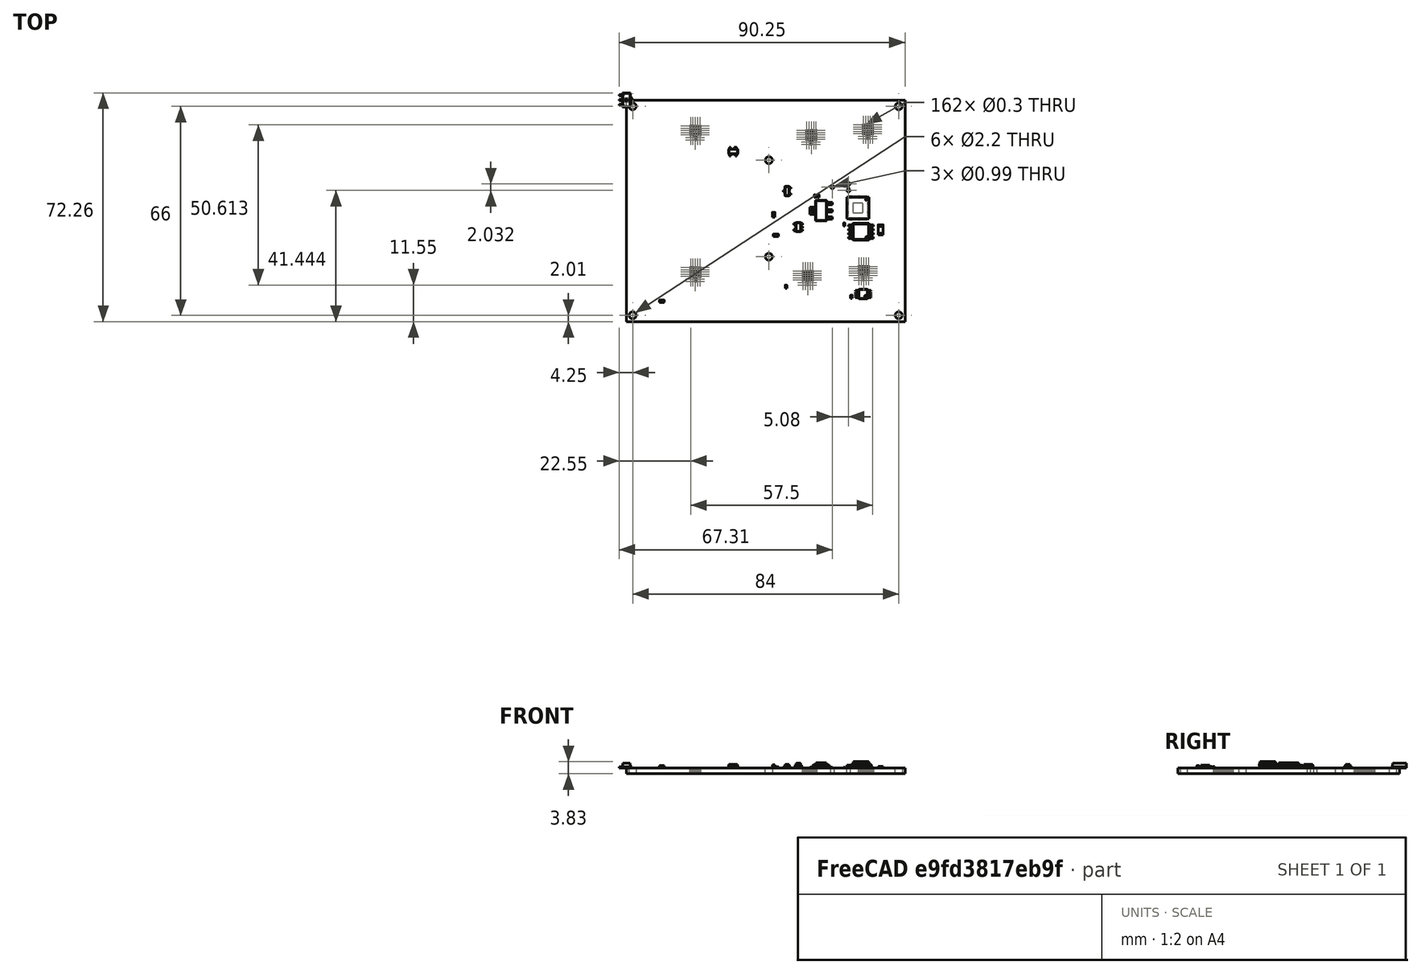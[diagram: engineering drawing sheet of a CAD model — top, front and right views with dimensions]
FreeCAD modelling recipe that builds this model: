
FCSTD DOCUMENT  (FreeCAD 2023.131R26244 +5365 (Git))
Label: FreeCAD_Render
License: All rights reserved
LicenseURL: http://en.wikipedia.org/wiki/All_rights_reserved
objects: App::Link×159, Part::Feature×25, App::Part×10, PartDesign::CoordinateSystem×1, Sketcher::SketchObject×1
note: 28 computed .brp shape members not serialized (recipe doc carries the construction recipe); baked Part::Feature solids carry a one-line shape summary decoded from their .brp

FEATURE [PartDesign::CoordinateSystem] Local_CS_5cf6
  AttacherType = Attacher::AttachEngine3D
  AttachmentSupport = -> [X_Axis]
  FixShape = 1
  InvalidShape = false
  MapMode = 2
  Support = -> [X_Axis]
  TreeRank = 4
  ValidateShape = false
FEATURE [Part::Feature] Pcb_5cf6
  FixShape = 1
  InvalidShape = false
  Placement = pos=(-99,65.045,0) rot=(0,0,1;0rad)
  TreeRank = 17
  ValidateShape = false
  shape: bbox 88 x 70 x 1.77 mm, 177 faces (baked)
FEATURE [Sketcher::SketchObject] PCB_Sketch_5cf6
  ArcFitTolerance = 1e-06
  ExternalBSplineMaxDegree = 5
  ExternalBSplineTolerance = 0.0001
  FixShape = 1
  FullyConstrained = false
  InternalTolerance = 1e-06
  InvalidShape = false
  MakeInternals = false
  TreeRank = 34
  ValidateShape = false
  sketch-geometry (4):
    g0: LineSegment StartX=0 StartY=-0.005 StartZ=0 EndX=88 EndY=-0.005 EndZ=0
    g1: LineSegment StartX=88 StartY=-0.005 StartZ=0 EndX=88 EndY=-70.005 EndZ=0
    g2: LineSegment StartX=88 StartY=-70.005 StartZ=0 EndX=0 EndY=-70.005 EndZ=0
    g3: LineSegment StartX=0 StartY=-70.005 StartZ=0 EndX=0 EndY=-0.005 EndZ=0
  constraints (4):
    c: Coincident(g2,g3)
    c: Coincident(g0,g3)
    c: Coincident(g1,g2)
    c: Coincident(g0,g1)
FEATURE [Part::Feature] Shape  label="R35_R_0402_1005Metric_f5f3ad6d96c7"
  FixShape = 1
  InvalidShape = false
  Placement = pos=(68.8,-39.325,0) rot=(0,0,-1;1.5708rad)
  TreeRank = 40
  ValidateShape = false
  shape: bbox 0.5 x 1 x 0.35 mm, 26 faces (baked)
FEATURE [App::Link] R35_R_0402_1005Metric_f5f3ad6d96c7_ln_  label="R9_R_0402_1005Metric_a21117af0435"
  AutoLinkLabel = true
  AutoPlacement = true
  LinkPlacement = pos=(48.15,-36.3,0) rot=(0,0,-1;1.5708rad)
  LinkedObject = -> Shape
  Placement = pos=(48.15,-36.3,0) rot=(0,0,-1;1.5708rad)
  SyncGroupVisibility = false
  TreeRank = 41
  _LinkVersion = 1
FEATURE [Part::Feature] Shape001  label="U27_MSOP_8_3x3mm_P065mm_f5ce7eb6c5d4"
  FixShape = 1
  InvalidShape = false
  Placement = pos=(74.7875,-61.275,0) rot=(0,0,1;3.14159rad)
  TreeRank = 43
  ValidateShape = false
  shape: bbox 4.9 x 3 x 0.95 mm, 156 faces (baked)
FEATURE [Part::Feature] Shape002  label="C12_C_0603_1608Metric_8642f7516920"
  FixShape = 1
  InvalidShape = false
  Placement = pos=(60.1,-30.35,0) rot=(0,0,1;3.14159rad)
  TreeRank = 45
  ValidateShape = false
  shape: bbox 1.6 x 0.8 x 0.8 mm, 28 faces (baked)
FEATURE [Part::Feature] Shape003  label="C99_C_0402_1005Metric_0b61def5e92b"
  FixShape = 1
  InvalidShape = false
  Placement = pos=(71.05,-62.125,0) rot=(0,0,-1;1.5708rad)
  TreeRank = 47
  ValidateShape = false
  shape: bbox 0.5 x 1 x 0.5 mm, 28 faces (baked)
FEATURE [App::Link] C99_C_0402_1005Metric_0b61def5e92b_ln_  label="C65_C_0402_1005Metric_039dcb1e20b4"
  AutoLinkLabel = true
  AutoPlacement = true
  LinkPlacement = pos=(50.435,-57.05,0) rot=(0,0,1;1.5708rad)
  LinkedObject = -> Shape003
  Placement = pos=(50.435,-57.05,0) rot=(0,0,1;1.5708rad)
  SyncGroupVisibility = false
  TreeRank = 48
  _LinkVersion = 1
FEATURE [App::Link] C12_C_0603_1608Metric_8642f7516920_ln_  label="C7_C_0603_1608Metric_5e726636510c"
  AutoLinkLabel = true
  AutoPlacement = true
  LinkPlacement = pos=(50.4,-40.35,0) rot=(0,0,-1;1.5708rad)
  LinkedObject = -> Shape002
  Placement = pos=(50.4,-40.35,0) rot=(0,0,-1;1.5708rad)
  SyncGroupVisibility = false
  TreeRank = 49
  _LinkVersion = 1
FEATURE [Part::Feature] Shape004  label="L20_L_0402_1005Metric_fefcc591d3d4"
  FixShape = 1
  InvalidShape = false
  Placement = pos=(50.435,-58.95,0) rot=(0,0,1;1.5708rad)
  TreeRank = 51
  ValidateShape = false
  shape: bbox 0.5 x 1 x 0.5 mm, 28 faces (baked)
FEATURE [App::Link] L20_L_0402_1005Metric_fefcc591d3d4_ln_  label="L12_L_0402_1005Metric_9afa7251a08a"
  AutoLinkLabel = true
  AutoPlacement = true
  LinkPlacement = pos=(51.02,-12,0) rot=(0,0,1;0rad)
  LinkedObject = -> Shape004
  Placement = pos=(51.02,-12,0) rot=(0,0,1;0rad)
  SyncGroupVisibility = false
  TreeRank = 52
  _LinkVersion = 1
FEATURE [App::Link] L20_L_0402_1005Metric_fefcc591d3d4_ln_001  label="L18_L_0402_1005Metric_8f30db38a927"
  AutoLinkLabel = true
  AutoPlacement = true
  LinkPlacement = pos=(47.085,-58,0) rot=(0,0,1;0rad)
  LinkedObject = -> Shape004
  Placement = pos=(47.085,-58,0) rot=(0,0,1;0rad)
  SyncGroupVisibility = false
  TreeRank = 53
  _LinkVersion = 1
FEATURE [App::Link] C99_C_0402_1005Metric_0b61def5e92b_ln_001  label="C32_C_0402_1005Metric_a150cae1aaa9"
  AutoLinkLabel = true
  AutoPlacement = true
  LinkPlacement = pos=(49.57,-11.05,0) rot=(0,0,1;1.5708rad)
  LinkedObject = -> Shape003
  Placement = pos=(49.57,-11.05,0) rot=(0,0,1;1.5708rad)
  SyncGroupVisibility = false
  TreeRank = 54
  _LinkVersion = 1
FEATURE [App::Link] C99_C_0402_1005Metric_0b61def5e92b_ln_002  label="C100_C_0402_1005Metric_bd74d8f4673b"
  AutoLinkLabel = true
  AutoPlacement = true
  LinkPlacement = pos=(78.5375,-60.455,0) rot=(0,0,-1;1.5708rad)
  LinkedObject = -> Shape003
  Placement = pos=(78.5375,-60.455,0) rot=(0,0,-1;1.5708rad)
  SyncGroupVisibility = false
  TreeRank = 55
  _LinkVersion = 1
FEATURE [App::Link] L20_L_0402_1005Metric_fefcc591d3d4_ln_002  label="L9_L_0402_1005Metric_ae438e03b951"
  AutoLinkLabel = true
  AutoPlacement = true
  LinkPlacement = pos=(46.22,-12,0) rot=(0,0,1;0rad)
  LinkedObject = -> Shape004
  Placement = pos=(46.22,-12,0) rot=(0,0,1;0rad)
  SyncGroupVisibility = false
  TreeRank = 56
  _LinkVersion = 1
FEATURE [App::Link] C12_C_0603_1608Metric_8642f7516920_ln_001  label="C57_C_0603_1608Metric_56c1fd1c9b26"
  AutoLinkLabel = true
  AutoPlacement = true
  LinkPlacement = pos=(25.875,-53.6,0) rot=(0,0,1;3.14159rad)
  LinkedObject = -> Shape002
  Placement = pos=(25.875,-53.6,0) rot=(0,0,1;3.14159rad)
  SyncGroupVisibility = false
  TreeRank = 57
  _LinkVersion = 1
FEATURE [Part::Feature] Shape005  label="D1_LED_0603_1608Metric_cfe29d252c61"
  FixShape = 1
  InvalidShape = false
  Placement = pos=(46.5,-36.2875,0) rot=(0,0,1;1.5708rad)
  TreeRank = 59
  ValidateShape = false
  shape: bbox 0.8 x 1.6 x 1.1 mm, 50 faces (baked)
FEATURE [Part::Feature] Shape006  label="R7_R_0603_1608Metric_f544fe8919fd"
  FixShape = 1
  InvalidShape = false
  Placement = pos=(47.225,-42.725,0) rot=(0,0,1;0rad)
  TreeRank = 61
  ValidateShape = false
  shape: bbox 1.6 x 0.8 x 0.45 mm, 26 faces (baked)
FEATURE [Part::Feature] Solid  label="adbeea57-9c39-11ed-93f0-dde97e994e83_part"
  FixShape = 1
  InvalidShape = false
  TreeRank = 75
  ValidateShape = false
  shape: bbox 2.5 x 4.5 x 1.5 mm, 12 faces (baked)
FEATURE [App::Part] Part  label="adbeea57-9c39-11ed-93f0-dde97e994e83"
  ClaimAllChildren = false
  ExportMode = 1
  Group = -> [Solid]
  Origin = -> Origin008
  TreeRank = 77
  _ExportChildren = -> [Solid]
  _GroupVersion = 1
FEATURE [Part::Feature] Solid001  label="adbeea58-9c39-11ed-93f0-dde97e994e83_part"
  FixShape = 1
  InvalidShape = false
  TreeRank = 78
  ValidateShape = false
  shape: bbox 2.5 x 1.6 x 0.4 mm, 12 faces (baked)
FEATURE [App::Part] Part001  label="adbeea58-9c39-11ed-93f0-dde97e994e83"
  ClaimAllChildren = false
  ExportMode = 1
  Group = -> [Solid001]
  Origin = -> Origin009
  TreeRank = 80
  _ExportChildren = -> [Solid001]
  _GroupVersion = 1
FEATURE [Part::Feature] Compound  label="adbeea59-9c39-11ed-93f0-dde97e994e83_part"
  FixShape = 1
  InvalidShape = false
  TreeRank = 81
  ValidateShape = false
  shape: bbox 1.5 x 3.4 x 0.4 mm, 18 faces, 3 solids (baked)
FEATURE [App::Part] Part002  label="adbeea59-9c39-11ed-93f0-dde97e994e83"
  ClaimAllChildren = false
  ExportMode = 1
  Group = -> [Compound]
  Origin = -> Origin010
  TreeRank = 83
  _ExportChildren = -> [Compound]
  _GroupVersion = 1
FEATURE [App::Part] Part003  label="adbeea56-9c39-11ed-93f0-dde97e994e83"
  ClaimAllChildren = false
  ExportMode = 1
  Group = -> [Part,Part001,Part002]
  Origin = -> Origin011
  TreeRank = 85
  _ExportChildren = -> [Part,Part001,Part002]
  _GroupVersion = 1
FEATURE [App::Part] Part004  label="U19_CQ assembly_0c48127af4d7"
  ClaimAllChildren = false
  ExportMode = 1
  Group = -> [Part003]
  Origin = -> Origin012
  Placement = pos=(57.3,-56.8,0) rot=(0,0,1;1.5708rad)
  TreeRank = 87
  _ExportChildren = -> [Part003]
  _GroupVersion = 1
FEATURE [Part::Feature] Shape007  label="U9_SOIC_8_5275x5275mm_P127mm_06fe98f0ee27"
  FixShape = 1
  InvalidShape = false
  Placement = pos=(74.1,-41.6,0) rot=(0,0,1;3.14159rad)
  TreeRank = 89
  ValidateShape = false
  shape: bbox 7.9 x 5.275 x 2.055 mm, 156 faces (baked)
FEATURE [App::Link] L20_L_0402_1005Metric_fefcc591d3d4_ln_003  label="L2_L_0402_1005Metric_494311214f8f"
  AutoLinkLabel = true
  AutoPlacement = true
  LinkPlacement = pos=(5.3,-14.185,0) rot=(0,0,1;1.5708rad)
  LinkedObject = -> Shape004
  Placement = pos=(5.3,-14.185,0) rot=(0,0,1;1.5708rad)
  SyncGroupVisibility = false
  TreeRank = 90
  _LinkVersion = 1
FEATURE [Part::Feature] Shape008  label="L6_L_0603_1608Metric_c72d023e8189"
  FixShape = 1
  InvalidShape = false
  Placement = pos=(11.2,-63.6,0) rot=(0,0,1;3.14159rad)
  TreeRank = 92
  ValidateShape = false
  shape: bbox 1.6 x 0.8 x 0.8 mm, 28 faces (baked)
FEATURE [Part::Feature] Shape009  label="U4_SOT_223_62a9cd10a710"
  FixShape = 1
  InvalidShape = false
  Placement = pos=(61.5,-34.95,0) rot=(0,0,1;3.14159rad)
  TreeRank = 94
  ValidateShape = false
  shape: bbox 7 x 6.5 x 1.7 mm, 78 faces (baked)
FEATURE [App::Link] U27_MSOP_8_3x3mm_P065mm_f5ce7eb6c5d4_ln_  label="U22_MSOP_8_3x3mm_P065mm_3038061a7a3b"
  AutoLinkLabel = true
  AutoPlacement = true
  LinkPlacement = pos=(76.3063,-16.625,0) rot=(0,0,1;3.14159rad)
  LinkedObject = -> Shape001
  Placement = pos=(76.3063,-16.625,0) rot=(0,0,1;3.14159rad)
  SyncGroupVisibility = false
  TreeRank = 95
  _LinkVersion = 1
FEATURE [App::Link] R7_R_0603_1608Metric_f544fe8919fd_ln_  label="R16_R_0603_1608Metric_eff10aa3adbc"
  AutoLinkLabel = true
  AutoPlacement = true
  LinkPlacement = pos=(54.025,-42.725,0) rot=(0,0,1;0rad)
  LinkedObject = -> Shape006
  Placement = pos=(54.025,-42.725,0) rot=(0,0,1;0rad)
  SyncGroupVisibility = false
  TreeRank = 96
  _LinkVersion = 1
FEATURE [App::Link] C99_C_0402_1005Metric_0b61def5e92b_ln_003  label="C72_C_0402_1005Metric_0a341764582e"
  AutoLinkLabel = true
  AutoPlacement = true
  LinkPlacement = pos=(18.3,-12.6,0) rot=(0,0,1;3.14159rad)
  LinkedObject = -> Shape003
  Placement = pos=(18.3,-12.6,0) rot=(0,0,1;3.14159rad)
  SyncGroupVisibility = false
  TreeRank = 97
  _LinkVersion = 1
FEATURE [App::Link] C99_C_0402_1005Metric_0b61def5e92b_ln_004  label="C42_C_0402_1005Metric_1668cc783fed"
  AutoLinkLabel = true
  AutoPlacement = true
  LinkPlacement = pos=(37.5,-57.9,0) rot=(0,0,1;0rad)
  LinkedObject = -> Shape003
  Placement = pos=(37.5,-57.9,0) rot=(0,0,1;0rad)
  SyncGroupVisibility = false
  TreeRank = 98
  _LinkVersion = 1
FEATURE [App::Link] C99_C_0402_1005Metric_0b61def5e92b_ln_005  label="C61_C_0402_1005Metric_119fb7f471d7"
  AutoLinkLabel = true
  AutoPlacement = true
  LinkPlacement = pos=(44.185,-58,0) rot=(0,0,1;0rad)
  LinkedObject = -> Shape003
  Placement = pos=(44.185,-58,0) rot=(0,0,1;0rad)
  SyncGroupVisibility = false
  TreeRank = 99
  _LinkVersion = 1
FEATURE [App::Link] R35_R_0402_1005Metric_f5f3ad6d96c7_ln_001  label="R12_R_0402_1005Metric_454fa87694b6"
  AutoLinkLabel = true
  AutoPlacement = true
  LinkPlacement = pos=(45.15,-33.2375,0) rot=(0,0,-1;1.5708rad)
  LinkedObject = -> Shape
  Placement = pos=(45.15,-33.2375,0) rot=(0,0,-1;1.5708rad)
  SyncGroupVisibility = false
  TreeRank = 100
  _LinkVersion = 1
FEATURE [App::Link] C99_C_0402_1005Metric_0b61def5e92b_ln_006  label="C41_C_0402_1005Metric_b9c80529164f"
  AutoLinkLabel = true
  AutoPlacement = true
  LinkPlacement = pos=(36.68,-12,0) rot=(0,0,1;0rad)
  LinkedObject = -> Shape003
  Placement = pos=(36.68,-12,0) rot=(0,0,1;0rad)
  SyncGroupVisibility = false
  TreeRank = 101
  _LinkVersion = 1
FEATURE [App::Link] L20_L_0402_1005Metric_fefcc591d3d4_ln_004  label="L17_L_0402_1005Metric_c09bc69e0e8d"
  AutoLinkLabel = true
  AutoPlacement = true
  LinkPlacement = pos=(45.635,-58.95,0) rot=(0,0,1;1.5708rad)
  LinkedObject = -> Shape004
  Placement = pos=(45.635,-58.95,0) rot=(0,0,1;1.5708rad)
  SyncGroupVisibility = false
  TreeRank = 102
  _LinkVersion = 1
FEATURE [App::Link] L20_L_0402_1005Metric_fefcc591d3d4_ln_005  label="L35_L_0402_1005Metric_862772697643"
  AutoLinkLabel = true
  AutoPlacement = true
  LinkPlacement = pos=(12.57,-55.965,0) rot=(0,0,1;1.5708rad)
  LinkedObject = -> Shape004
  Placement = pos=(12.57,-55.965,0) rot=(0,0,1;1.5708rad)
  SyncGroupVisibility = false
  TreeRank = 103
  _LinkVersion = 1
FEATURE [App::Link] C99_C_0402_1005Metric_0b61def5e92b_ln_007  label="C94_C_0402_1005Metric_5b9e6d4c6d4e"
  AutoLinkLabel = true
  AutoPlacement = true
  LinkPlacement = pos=(12.57,-58.63,0) rot=(0,0,1;1.5708rad)
  LinkedObject = -> Shape003
  Placement = pos=(12.57,-58.63,0) rot=(0,0,1;1.5708rad)
  SyncGroupVisibility = false
  TreeRank = 104
  _LinkVersion = 1
FEATURE [App::Link] C99_C_0402_1005Metric_0b61def5e92b_ln_008  label="C17_C_0402_1005Metric_572786f3d237"
  AutoLinkLabel = true
  AutoPlacement = true
  LinkPlacement = pos=(66.78,-44.5,0) rot=(0,0,1;0rad)
  LinkedObject = -> Shape003
  Placement = pos=(66.78,-44.5,0) rot=(0,0,1;0rad)
  SyncGroupVisibility = false
  TreeRank = 105
  _LinkVersion = 1
FEATURE [App::Link] R35_R_0402_1005Metric_f5f3ad6d96c7_ln_002  label="R15_R_0402_1005Metric_dd92e1eecf5b"
  AutoLinkLabel = true
  AutoPlacement = true
  LinkPlacement = pos=(54.15,-33.2775,0) rot=(0,0,-1;1.5708rad)
  LinkedObject = -> Shape
  Placement = pos=(54.15,-33.2775,0) rot=(0,0,-1;1.5708rad)
  SyncGroupVisibility = false
  TreeRank = 106
  _LinkVersion = 1
FEATURE [App::Link] C12_C_0603_1608Metric_8642f7516920_ln_002  label="C16_C_0603_1608Metric_42011b40d980"
  AutoLinkLabel = true
  AutoPlacement = true
  LinkPlacement = pos=(6.3,-15.9,0) rot=(0,0,1;3.14159rad)
  LinkedObject = -> Shape002
  Placement = pos=(6.3,-15.9,0) rot=(0,0,1;3.14159rad)
  SyncGroupVisibility = false
  TreeRank = 107
  _LinkVersion = 1
FEATURE [App::Link] C99_C_0402_1005Metric_0b61def5e92b_ln_009  label="C38_C_0402_1005Metric_071abb743ee5"
  AutoLinkLabel = true
  AutoPlacement = true
  LinkPlacement = pos=(26.4,-12.6,0) rot=(0,0,1;3.14159rad)
  LinkedObject = -> Shape003
  Placement = pos=(26.4,-12.6,0) rot=(0,0,1;3.14159rad)
  SyncGroupVisibility = false
  TreeRank = 108
  _LinkVersion = 1
FEATURE [App::Link] L20_L_0402_1005Metric_fefcc591d3d4_ln_006  label="L28_L_0402_1005Metric_31be49f92a08"
  AutoLinkLabel = true
  AutoPlacement = true
  LinkPlacement = pos=(9.6,-35,0) rot=(0,0,1;0rad)
  LinkedObject = -> Shape004
  Placement = pos=(9.6,-35,0) rot=(0,0,1;0rad)
  SyncGroupVisibility = false
  TreeRank = 109
  _LinkVersion = 1
FEATURE [App::Link] L20_L_0402_1005Metric_fefcc591d3d4_ln_007  label="L16_L_0402_1005Metric_a015a0d61d6a"
  AutoLinkLabel = true
  AutoPlacement = true
  LinkPlacement = pos=(42.285,-58,0) rot=(0,0,1;0rad)
  LinkedObject = -> Shape004
  Placement = pos=(42.285,-58,0) rot=(0,0,1;0rad)
  SyncGroupVisibility = false
  TreeRank = 110
  _LinkVersion = 1
FEATURE [App::Link] C99_C_0402_1005Metric_0b61def5e92b_ln_010  label="C91_C_0402_1005Metric_d935b4825f22"
  AutoLinkLabel = true
  AutoPlacement = true
  LinkPlacement = pos=(11.05,-34.52,0) rot=(0,0,1;1.5708rad)
  LinkedObject = -> Shape003
  Placement = pos=(11.05,-34.52,0) rot=(0,0,1;1.5708rad)
  SyncGroupVisibility = false
  TreeRank = 111
  _LinkVersion = 1
FEATURE [App::Link] C12_C_0603_1608Metric_8642f7516920_ln_003  label="C10_C_0603_1608Metric_9efa6503c595"
  AutoLinkLabel = true
  AutoPlacement = true
  LinkPlacement = pos=(53.4625,-28.575,0) rot=(0,0,1;1.5708rad)
  LinkedObject = -> Shape002
  Placement = pos=(53.4625,-28.575,0) rot=(0,0,1;1.5708rad)
  SyncGroupVisibility = false
  TreeRank = 112
  _LinkVersion = 1
FEATURE [App::Link] R35_R_0402_1005Metric_f5f3ad6d96c7_ln_003  label="R24_R_0402_1005Metric_d04b1966e5ee"
  AutoLinkLabel = true
  AutoPlacement = true
  LinkPlacement = pos=(12.8,-36.51,0) rot=(0,0,1;1.5708rad)
  LinkedObject = -> Shape
  Placement = pos=(12.8,-36.51,0) rot=(0,0,1;1.5708rad)
  SyncGroupVisibility = false
  TreeRank = 113
  _LinkVersion = 1
FEATURE [App::Link] L20_L_0402_1005Metric_fefcc591d3d4_ln_008  label="L32_L_0402_1005Metric_198f0760abc9"
  AutoLinkLabel = true
  AutoPlacement = true
  LinkPlacement = pos=(6.885,-57.3,0) rot=(0,0,1;0rad)
  LinkedObject = -> Shape004
  Placement = pos=(6.885,-57.3,0) rot=(0,0,1;0rad)
  SyncGroupVisibility = false
  TreeRank = 114
  _LinkVersion = 1
FEATURE [App::Link] L20_L_0402_1005Metric_fefcc591d3d4_ln_009  label="L3_L_0402_1005Metric_fcb539355568"
  AutoLinkLabel = true
  AutoPlacement = true
  LinkPlacement = pos=(24.9,-12.115,0) rot=(0,0,-1;1.5708rad)
  LinkedObject = -> Shape004
  Placement = pos=(24.9,-12.115,0) rot=(0,0,-1;1.5708rad)
  SyncGroupVisibility = false
  TreeRank = 115
  _LinkVersion = 1
FEATURE [App::Link] C99_C_0402_1005Metric_0b61def5e92b_ln_011  label="C64_C_0402_1005Metric_0c6ecc967038"
  AutoLinkLabel = true
  AutoPlacement = true
  LinkPlacement = pos=(48.985,-58,0) rot=(0,0,1;0rad)
  LinkedObject = -> Shape003
  Placement = pos=(48.985,-58,0) rot=(0,0,1;0rad)
  SyncGroupVisibility = false
  TreeRank = 116
  _LinkVersion = 1
FEATURE [App::Link] U19_CQ_assembly_0c48127af4d7_ln_  label="U15_CQ assembly_a8ecb2b2cfc9"
  AutoLinkLabel = true
  AutoPlacement = true
  LinkPlacement = pos=(76.3,-10.55,0) rot=(0,0,1;1.5708rad)
  LinkedObject = -> Part004
  Placement = pos=(76.3,-10.55,0) rot=(0,0,1;1.5708rad)
  SyncGroupVisibility = false
  TreeRank = 117
  _LinkVersion = 1
FEATURE [App::Link] C12_C_0603_1608Metric_8642f7516920_ln_004  label="C56_C_0603_1608Metric_def960d6d94d"
  AutoLinkLabel = true
  AutoPlacement = true
  LinkPlacement = pos=(80.375,-7.265,0) rot=(0,0,1;3.14159rad)
  LinkedObject = -> Shape002
  Placement = pos=(80.375,-7.265,0) rot=(0,0,1;3.14159rad)
  SyncGroupVisibility = false
  TreeRank = 118
  _LinkVersion = 1
FEATURE [App::Link] R35_R_0402_1005Metric_f5f3ad6d96c7_ln_004  label="R18_R_0402_1005Metric_c2070ab9652d"
  AutoLinkLabel = true
  AutoPlacement = true
  LinkPlacement = pos=(81.6,-18.11,0) rot=(0,0,1;1.5708rad)
  LinkedObject = -> Shape
  Placement = pos=(81.6,-18.11,0) rot=(0,0,1;1.5708rad)
  SyncGroupVisibility = false
  TreeRank = 119
  _LinkVersion = 1
FEATURE [App::Link] C99_C_0402_1005Metric_0b61def5e92b_ln_012  label="C15_C_0402_1005Metric_dfbf553078c1"
  AutoLinkLabel = true
  AutoPlacement = true
  LinkPlacement = pos=(68.7,-43.98,0) rot=(0,0,-1;1.5708rad)
  LinkedObject = -> Shape003
  Placement = pos=(68.7,-43.98,0) rot=(0,0,-1;1.5708rad)
  SyncGroupVisibility = false
  TreeRank = 120
  _LinkVersion = 1
FEATURE [App::Link] D1_LED_0603_1608Metric_cfe29d252c61_ln_  label="D2_LED_0603_1608Metric_e46dc4190c8f"
  AutoLinkLabel = true
  AutoPlacement = true
  LinkPlacement = pos=(49.5,-36.2875,0) rot=(0,0,1;1.5708rad)
  LinkedObject = -> Shape005
  Placement = pos=(49.5,-36.2875,0) rot=(0,0,1;1.5708rad)
  SyncGroupVisibility = false
  TreeRank = 121
  _LinkVersion = 1
FEATURE [App::Link] L20_L_0402_1005Metric_fefcc591d3d4_ln_010  label="L10_L_0402_1005Metric_c9969f9a3005"
  AutoLinkLabel = true
  AutoPlacement = true
  LinkPlacement = pos=(78.01,-56.7925,0) rot=(0,0,-1;1.5708rad)
  LinkedObject = -> Shape004
  Placement = pos=(78.01,-56.7925,0) rot=(0,0,-1;1.5708rad)
  SyncGroupVisibility = false
  TreeRank = 122
  _LinkVersion = 1
FEATURE [App::Link] L20_L_0402_1005Metric_fefcc591d3d4_ln_011  label="L37_L_0402_1005Metric_2736a4dceb44"
  AutoLinkLabel = true
  AutoPlacement = true
  LinkPlacement = pos=(15.17,-55.965,0) rot=(0,0,1;1.5708rad)
  LinkedObject = -> Shape004
  Placement = pos=(15.17,-55.965,0) rot=(0,0,1;1.5708rad)
  SyncGroupVisibility = false
  TreeRank = 123
  _LinkVersion = 1
FEATURE [App::Link] C12_C_0603_1608Metric_8642f7516920_ln_005  label="C9_C_0603_1608Metric_568df7630068"
  AutoLinkLabel = true
  AutoPlacement = true
  LinkPlacement = pos=(64.425,-30.35,0) rot=(0,0,1;0rad)
  LinkedObject = -> Shape002
  Placement = pos=(64.425,-30.35,0) rot=(0,0,1;0rad)
  SyncGroupVisibility = false
  TreeRank = 124
  _LinkVersion = 1
FEATURE [App::Link] C99_C_0402_1005Metric_0b61def5e92b_ln_013  label="C63_C_0402_1005Metric_87cdc0513b1c"
  AutoLinkLabel = true
  AutoPlacement = true
  LinkPlacement = pos=(72.75,-12.0394,0) rot=(0,0,-1;0.785398rad)
  LinkedObject = -> Shape003
  Placement = pos=(72.75,-12.0394,0) rot=(0,0,-1;0.785398rad)
  SyncGroupVisibility = false
  TreeRank = 125
  _LinkVersion = 1
FEATURE [App::Link] L20_L_0402_1005Metric_fefcc591d3d4_ln_012  label="L22_L_0402_1005Metric_491585082001"
  AutoLinkLabel = true
  AutoPlacement = true
  LinkPlacement = pos=(11.255,-12.6,0) rot=(0,0,1;0rad)
  LinkedObject = -> Shape004
  Placement = pos=(11.255,-12.6,0) rot=(0,0,1;0rad)
  SyncGroupVisibility = false
  TreeRank = 126
  _LinkVersion = 1
FEATURE [App::Link] C12_C_0603_1608Metric_8642f7516920_ln_006  label="C101_C_0603_1608Metric_0d3315560940"
  AutoLinkLabel = true
  AutoPlacement = true
  LinkPlacement = pos=(6.325,-62.1,0) rot=(0,0,1;3.14159rad)
  LinkedObject = -> Shape002
  Placement = pos=(6.325,-62.1,0) rot=(0,0,1;3.14159rad)
  SyncGroupVisibility = false
  TreeRank = 127
  _LinkVersion = 1
FEATURE [App::Link] D1_LED_0603_1608Metric_cfe29d252c61_ln_001  label="D6_LED_0603_1608Metric_c5920ca47e15"
  AutoLinkLabel = true
  AutoPlacement = true
  LinkPlacement = pos=(49.5,-33.25,0) rot=(0,0,1;1.5708rad)
  LinkedObject = -> Shape005
  Placement = pos=(49.5,-33.25,0) rot=(0,0,1;1.5708rad)
  SyncGroupVisibility = false
  TreeRank = 128
  _LinkVersion = 1
FEATURE [App::Link] R7_R_0603_1608Metric_f544fe8919fd_ln_001  label="R6_R_0603_1608Metric_ad8729a0a211"
  AutoLinkLabel = true
  AutoPlacement = true
  LinkPlacement = pos=(58.8,-40.3,0) rot=(0,0,-1;1.5708rad)
  LinkedObject = -> Shape006
  Placement = pos=(58.8,-40.3,0) rot=(0,0,-1;1.5708rad)
  SyncGroupVisibility = false
  TreeRank = 129
  _LinkVersion = 1
FEATURE [App::Link] C99_C_0402_1005Metric_0b61def5e92b_ln_014  label="C85_C_0402_1005Metric_55c8310b5d15"
  AutoLinkLabel = true
  AutoPlacement = true
  LinkPlacement = pos=(72.5687,-17.475,0) rot=(0,0,-1;1.5708rad)
  LinkedObject = -> Shape003
  Placement = pos=(72.5687,-17.475,0) rot=(0,0,-1;1.5708rad)
  SyncGroupVisibility = false
  TreeRank = 130
  _LinkVersion = 1
FEATURE [App::Link] L20_L_0402_1005Metric_fefcc591d3d4_ln_013  label="L19_L_0402_1005Metric_5587f70061e4"
  AutoLinkLabel = true
  AutoPlacement = true
  LinkPlacement = pos=(79.7,-12.115,0) rot=(0,0,-1;1.5708rad)
  LinkedObject = -> Shape004
  Placement = pos=(79.7,-12.115,0) rot=(0,0,-1;1.5708rad)
  SyncGroupVisibility = false
  TreeRank = 131
  _LinkVersion = 1
FEATURE [App::Link] C12_C_0603_1608Metric_8642f7516920_ln_007  label="C5_C_0603_1608Metric_b7c57633a563"
  AutoLinkLabel = true
  AutoPlacement = true
  LinkPlacement = pos=(25.875,-8.9,0) rot=(0,0,1;3.14159rad)
  LinkedObject = -> Shape002
  Placement = pos=(25.875,-8.9,0) rot=(0,0,1;3.14159rad)
  SyncGroupVisibility = false
  TreeRank = 132
  _LinkVersion = 1
FEATURE [App::Link] L20_L_0402_1005Metric_fefcc591d3d4_ln_014  label="L27_L_0402_1005Metric_34f9cab72f46"
  AutoLinkLabel = true
  AutoPlacement = true
  LinkPlacement = pos=(6.7,-35,0) rot=(0,0,1;0rad)
  LinkedObject = -> Shape004
  Placement = pos=(6.7,-35,0) rot=(0,0,1;0rad)
  SyncGroupVisibility = false
  TreeRank = 133
  _LinkVersion = 1
FEATURE [App::Link] C12_C_0603_1608Metric_8642f7516920_ln_008  label="C87_C_0603_1608Metric_3d10d2c6202e"
  AutoLinkLabel = true
  AutoPlacement = true
  LinkPlacement = pos=(79.025,-55.0725,0) rot=(0,0,1;3.14159rad)
  LinkedObject = -> Shape002
  Placement = pos=(79.025,-55.0725,0) rot=(0,0,1;3.14159rad)
  SyncGroupVisibility = false
  TreeRank = 134
  _LinkVersion = 1
FEATURE [App::Link] L20_L_0402_1005Metric_fefcc591d3d4_ln_015  label="L13_L_0402_1005Metric_fe637daa8a0d"
  AutoLinkLabel = true
  AutoPlacement = true
  LinkPlacement = pos=(6.885,-12.6,0) rot=(0,0,1;0rad)
  LinkedObject = -> Shape004
  Placement = pos=(6.885,-12.6,0) rot=(0,0,1;0rad)
  SyncGroupVisibility = false
  TreeRank = 135
  _LinkVersion = 1
FEATURE [App::Link] C12_C_0603_1608Metric_8642f7516920_ln_009  label="C40_C_0603_1608Metric_611b7b94bbb0"
  AutoLinkLabel = true
  AutoPlacement = true
  LinkPlacement = pos=(25.875,-52.1,0) rot=(0,0,1;3.14159rad)
  LinkedObject = -> Shape002
  Placement = pos=(25.875,-52.1,0) rot=(0,0,1;3.14159rad)
  SyncGroupVisibility = false
  TreeRank = 136
  _LinkVersion = 1
FEATURE [App::Link] R35_R_0402_1005Metric_f5f3ad6d96c7_ln_005  label="R38_R_0402_1005Metric_850526eb3a70"
  AutoLinkLabel = true
  AutoPlacement = true
  LinkPlacement = pos=(80.0813,-62.76,0) rot=(0,0,1;1.5708rad)
  LinkedObject = -> Shape
  Placement = pos=(80.0813,-62.76,0) rot=(0,0,1;1.5708rad)
  SyncGroupVisibility = false
  TreeRank = 137
  _LinkVersion = 1
FEATURE [App::Link] C99_C_0402_1005Metric_0b61def5e92b_ln_015  label="C93_C_0402_1005Metric_9b432eb8458a"
  AutoLinkLabel = true
  AutoPlacement = true
  LinkPlacement = pos=(9.97,-58.63,0) rot=(0,0,1;1.5708rad)
  LinkedObject = -> Shape003
  Placement = pos=(9.97,-58.63,0) rot=(0,0,1;1.5708rad)
  SyncGroupVisibility = false
  TreeRank = 138
  _LinkVersion = 1
FEATURE [App::Link] C12_C_0603_1608Metric_8642f7516920_ln_010  label="C60_C_0603_1608Metric_aafec61e4182"
  AutoLinkLabel = true
  AutoPlacement = true
  LinkPlacement = pos=(25.875,-55.1,0) rot=(0,0,1;3.14159rad)
  LinkedObject = -> Shape002
  Placement = pos=(25.875,-55.1,0) rot=(0,0,1;3.14159rad)
  SyncGroupVisibility = false
  TreeRank = 139
  _LinkVersion = 1
FEATURE [App::Link] C12_C_0603_1608Metric_8642f7516920_ln_011  label="C74_C_0603_1608Metric_09ec40bea9be"
  AutoLinkLabel = true
  AutoPlacement = true
  LinkPlacement = pos=(62.565,-9.135,0) rot=(0,0,1;3.14159rad)
  LinkedObject = -> Shape002
  Placement = pos=(62.565,-9.135,0) rot=(0,0,1;3.14159rad)
  SyncGroupVisibility = false
  TreeRank = 140
  _LinkVersion = 1
FEATURE [App::Link] C12_C_0603_1608Metric_8642f7516920_ln_012  label="C102_C_0603_1608Metric_fbca4f1203a4"
  AutoLinkLabel = true
  AutoPlacement = true
  LinkPlacement = pos=(6.325,-60.6,0) rot=(0,0,1;3.14159rad)
  LinkedObject = -> Shape002
  Placement = pos=(6.325,-60.6,0) rot=(0,0,1;3.14159rad)
  SyncGroupVisibility = false
  TreeRank = 141
  _LinkVersion = 1
FEATURE [App::Link] C99_C_0402_1005Metric_0b61def5e92b_ln_016  label="C95_C_0402_1005Metric_b8fe9a8e5a91"
  AutoLinkLabel = true
  AutoPlacement = true
  LinkPlacement = pos=(15.17,-58.63,0) rot=(0,0,1;1.5708rad)
  LinkedObject = -> Shape003
  Placement = pos=(15.17,-58.63,0) rot=(0,0,1;1.5708rad)
  SyncGroupVisibility = false
  TreeRank = 142
  _LinkVersion = 1
FEATURE [App::Link] D1_LED_0603_1608Metric_cfe29d252c61_ln_002  label="D8_LED_0603_1608Metric_bad8365d5fa2"
  AutoLinkLabel = true
  AutoPlacement = true
  LinkPlacement = pos=(55.5,-33.25,0) rot=(0,0,1;1.5708rad)
  LinkedObject = -> Shape005
  Placement = pos=(55.5,-33.25,0) rot=(0,0,1;1.5708rad)
  SyncGroupVisibility = false
  TreeRank = 143
  _LinkVersion = 1
FEATURE [App::Link] C99_C_0402_1005Metric_0b61def5e92b_ln_017  label="C89_C_0402_1005Metric_912ed4a3e6aa"
  AutoLinkLabel = true
  AutoPlacement = true
  LinkPlacement = pos=(5.25,-34.52,0) rot=(0,0,1;1.5708rad)
  LinkedObject = -> Shape003
  Placement = pos=(5.25,-34.52,0) rot=(0,0,1;1.5708rad)
  SyncGroupVisibility = false
  TreeRank = 144
  _LinkVersion = 1
FEATURE [App::Link] L20_L_0402_1005Metric_fefcc591d3d4_ln_016  label="L30_L_0402_1005Metric_7c5d0824e401"
  AutoLinkLabel = true
  AutoPlacement = true
  LinkPlacement = pos=(15.17,-11.265,0) rot=(0,0,1;1.5708rad)
  LinkedObject = -> Shape004
  Placement = pos=(15.17,-11.265,0) rot=(0,0,1;1.5708rad)
  SyncGroupVisibility = false
  TreeRank = 145
  _LinkVersion = 1
FEATURE [App::Link] L20_L_0402_1005Metric_fefcc591d3d4_ln_017  label="L7_L_0402_1005Metric_456bcb2105ab"
  AutoLinkLabel = true
  AutoPlacement = true
  LinkPlacement = pos=(44.77,-12.95,0) rot=(0,0,1;1.5708rad)
  LinkedObject = -> Shape004
  Placement = pos=(44.77,-12.95,0) rot=(0,0,1;1.5708rad)
  SyncGroupVisibility = false
  TreeRank = 146
  _LinkVersion = 1
FEATURE [App::Link] C12_C_0603_1608Metric_8642f7516920_ln_013  label="C76_C_0603_1608Metric_3a528c4e4e0e"
  AutoLinkLabel = true
  AutoPlacement = true
  LinkPlacement = pos=(61.375,-56.7,0) rot=(0,0,1;3.14159rad)
  LinkedObject = -> Shape002
  Placement = pos=(61.375,-56.7,0) rot=(0,0,1;3.14159rad)
  SyncGroupVisibility = false
  TreeRank = 147
  _LinkVersion = 1
FEATURE [App::Link] C99_C_0402_1005Metric_0b61def5e92b_ln_018  label="C4_C_0402_1005Metric_44e2dd5ad2b2"
  AutoLinkLabel = true
  AutoPlacement = true
  LinkPlacement = pos=(8.7,-12.6,0) rot=(0,0,1;3.14159rad)
  LinkedObject = -> Shape003
  Placement = pos=(8.7,-12.6,0) rot=(0,0,1;3.14159rad)
  SyncGroupVisibility = false
  TreeRank = 148
  _LinkVersion = 1
FEATURE [App::Link] R35_R_0402_1005Metric_f5f3ad6d96c7_ln_006  label="R25_R_0402_1005Metric_d01a4dbf24dd"
  AutoLinkLabel = true
  AutoPlacement = true
  LinkPlacement = pos=(11.3,-37,0) rot=(0,0,1;0rad)
  LinkedObject = -> Shape
  Placement = pos=(11.3,-37,0) rot=(0,0,1;0rad)
  SyncGroupVisibility = false
  TreeRank = 149
  _LinkVersion = 1
FEATURE [App::Link] C99_C_0402_1005Metric_0b61def5e92b_ln_019  label="C62_C_0402_1005Metric_ef4612ef1b06"
  AutoLinkLabel = true
  AutoPlacement = true
  LinkPlacement = pos=(45.635,-57.05,0) rot=(0,0,1;1.5708rad)
  LinkedObject = -> Shape003
  Placement = pos=(45.635,-57.05,0) rot=(0,0,1;1.5708rad)
  SyncGroupVisibility = false
  TreeRank = 150
  _LinkVersion = 1
FEATURE [App::Link] C99_C_0402_1005Metric_0b61def5e92b_ln_020  label="C67_C_0402_1005Metric_c4b910a4755d"
  AutoLinkLabel = true
  AutoPlacement = true
  LinkPlacement = pos=(53.785,-58,0) rot=(0,0,1;0rad)
  LinkedObject = -> Shape003
  Placement = pos=(53.785,-58,0) rot=(0,0,1;0rad)
  SyncGroupVisibility = false
  TreeRank = 151
  _LinkVersion = 1
FEATURE [Part::Feature] Shape010  label="F1_Fuse_1206_3216Metric_ddd44b4a31ef"
  FixShape = 1
  InvalidShape = false
  Placement = pos=(80.3,-41,0) rot=(0,0,-1;1.5708rad)
  TreeRank = 153
  ValidateShape = false
  shape: bbox 1.6 x 3.2 x 0.55 mm, 26 faces (baked)
FEATURE [App::Link] L20_L_0402_1005Metric_fefcc591d3d4_ln_018  label="L26_L_0402_1005Metric_0ac06aa6dc64"
  AutoLinkLabel = true
  AutoPlacement = true
  LinkPlacement = pos=(60.4,-58.415,0) rot=(0,0,-1;1.5708rad)
  LinkedObject = -> Shape004
  Placement = pos=(60.4,-58.415,0) rot=(0,0,-1;1.5708rad)
  SyncGroupVisibility = false
  TreeRank = 154
  _LinkVersion = 1
FEATURE [App::Link] C99_C_0402_1005Metric_0b61def5e92b_ln_021  label="C96_C_0402_1005Metric_12cca5f82af4"
  AutoLinkLabel = true
  AutoPlacement = true
  LinkPlacement = pos=(18.3,-57.3,0) rot=(0,0,1;3.14159rad)
  LinkedObject = -> Shape003
  Placement = pos=(18.3,-57.3,0) rot=(0,0,1;3.14159rad)
  SyncGroupVisibility = false
  TreeRank = 155
  _LinkVersion = 1
FEATURE [App::Link] C99_C_0402_1005Metric_0b61def5e92b_ln_022  label="C97_C_0402_1005Metric_f17c20ed1adf"
  AutoLinkLabel = true
  AutoPlacement = true
  LinkPlacement = pos=(77.3,-28.5,0) rot=(0,0,1;1.5708rad)
  LinkedObject = -> Shape003
  Placement = pos=(77.3,-28.5,0) rot=(0,0,1;1.5708rad)
  SyncGroupVisibility = false
  TreeRank = 156
  _LinkVersion = 1
FEATURE [App::Link] L20_L_0402_1005Metric_fefcc591d3d4_ln_019  label="L14_L_0402_1005Metric_1540f4a361fb"
  AutoLinkLabel = true
  AutoPlacement = true
  LinkPlacement = pos=(9.97,-11.265,0) rot=(0,0,1;1.5708rad)
  LinkedObject = -> Shape004
  Placement = pos=(9.97,-11.265,0) rot=(0,0,1;1.5708rad)
  SyncGroupVisibility = false
  TreeRank = 157
  _LinkVersion = 1
FEATURE [App::Link] C99_C_0402_1005Metric_0b61def5e92b_ln_023  label="C92_C_0402_1005Metric_180eef45c809"
  AutoLinkLabel = true
  AutoPlacement = true
  LinkPlacement = pos=(8.7,-57.3,0) rot=(0,0,1;3.14159rad)
  LinkedObject = -> Shape003
  Placement = pos=(8.7,-57.3,0) rot=(0,0,1;3.14159rad)
  SyncGroupVisibility = false
  TreeRank = 158
  _LinkVersion = 1
FEATURE [App::Link] R35_R_0402_1005Metric_f5f3ad6d96c7_ln_007  label="R13_R_0402_1005Metric_2d540afb9262"
  AutoLinkLabel = true
  AutoPlacement = true
  LinkPlacement = pos=(48.15,-33.2875,0) rot=(0,0,-1;1.5708rad)
  LinkedObject = -> Shape
  Placement = pos=(48.15,-33.2875,0) rot=(0,0,-1;1.5708rad)
  SyncGroupVisibility = false
  TreeRank = 159
  _LinkVersion = 1
FEATURE [App::Link] C99_C_0402_1005Metric_0b61def5e92b_ln_024  label="C30_C_0402_1005Metric_0f836c2fbbcc"
  AutoLinkLabel = true
  AutoPlacement = true
  LinkPlacement = pos=(44.77,-11.05,0) rot=(0,0,1;1.5708rad)
  LinkedObject = -> Shape003
  Placement = pos=(44.77,-11.05,0) rot=(0,0,1;1.5708rad)
  SyncGroupVisibility = false
  TreeRank = 160
  _LinkVersion = 1
FEATURE [App::Link] L20_L_0402_1005Metric_fefcc591d3d4_ln_020  label="L21_L_0402_1005Metric_c7900d6e66f0"
  AutoLinkLabel = true
  AutoPlacement = true
  LinkPlacement = pos=(51.885,-58,0) rot=(0,0,1;0rad)
  LinkedObject = -> Shape004
  Placement = pos=(51.885,-58,0) rot=(0,0,1;0rad)
  SyncGroupVisibility = false
  TreeRank = 161
  _LinkVersion = 1
FEATURE [App::Link] C99_C_0402_1005Metric_0b61def5e92b_ln_025  label="C73_C_0402_1005Metric_c90faed0705e"
  AutoLinkLabel = true
  AutoPlacement = true
  LinkPlacement = pos=(26.4,-57.3,0) rot=(0,0,1;3.14159rad)
  LinkedObject = -> Shape003
  Placement = pos=(26.4,-57.3,0) rot=(0,0,1;3.14159rad)
  SyncGroupVisibility = false
  TreeRank = 162
  _LinkVersion = 1
FEATURE [App::Link] C99_C_0402_1005Metric_0b61def5e92b_ln_026  label="C77_C_0402_1005Metric_efc5d86ffb13"
  AutoLinkLabel = true
  AutoPlacement = true
  LinkPlacement = pos=(63.5,-57.9,0) rot=(0,0,1;0.785398rad)
  LinkedObject = -> Shape003
  Placement = pos=(63.5,-57.9,0) rot=(0,0,1;0.785398rad)
  SyncGroupVisibility = false
  TreeRank = 163
  _LinkVersion = 1
FEATURE [App::Link] C99_C_0402_1005Metric_0b61def5e92b_ln_027  label="C54_C_0402_1005Metric_30c834f8864e"
  AutoLinkLabel = true
  AutoPlacement = true
  LinkPlacement = pos=(79.49,-57.2725,0) rot=(0,0,1;0rad)
  LinkedObject = -> Shape003
  Placement = pos=(79.49,-57.2725,0) rot=(0,0,1;0rad)
  SyncGroupVisibility = false
  TreeRank = 164
  _LinkVersion = 1
FEATURE [App::Link] C12_C_0603_1608Metric_8642f7516920_ln_014  label="C8_C_0603_1608Metric_8e5024c1359d"
  AutoLinkLabel = true
  AutoPlacement = true
  LinkPlacement = pos=(48.0625,-28.575,0) rot=(0,0,-1;1.5708rad)
  LinkedObject = -> Shape002
  Placement = pos=(48.0625,-28.575,0) rot=(0,0,-1;1.5708rad)
  SyncGroupVisibility = false
  TreeRank = 165
  _LinkVersion = 1
FEATURE [App::Link] C99_C_0402_1005Metric_0b61def5e92b_ln_028  label="C36_C_0402_1005Metric_1f751e97ced4"
  AutoLinkLabel = true
  AutoPlacement = true
  LinkPlacement = pos=(34.48,-24.2,0) rot=(0,0,1;0rad)
  LinkedObject = -> Shape003
  Placement = pos=(34.48,-24.2,0) rot=(0,0,1;0rad)
  SyncGroupVisibility = false
  TreeRank = 166
  _LinkVersion = 1
FEATURE [App::Link] C99_C_0402_1005Metric_0b61def5e92b_ln_029  label="C90_C_0402_1005Metric_35b60444df71"
  AutoLinkLabel = true
  AutoPlacement = true
  LinkPlacement = pos=(8.15,-34.52,0) rot=(0,0,1;1.5708rad)
  LinkedObject = -> Shape003
  Placement = pos=(8.15,-34.52,0) rot=(0,0,1;1.5708rad)
  SyncGroupVisibility = false
  TreeRank = 167
  _LinkVersion = 1
FEATURE [App::Link] C99_C_0402_1005Metric_0b61def5e92b_ln_030  label="C31_C_0402_1005Metric_ea5578401aff"
  AutoLinkLabel = true
  AutoPlacement = true
  LinkPlacement = pos=(48.12,-12,0) rot=(0,0,1;0rad)
  LinkedObject = -> Shape003
  Placement = pos=(48.12,-12,0) rot=(0,0,1;0rad)
  SyncGroupVisibility = false
  TreeRank = 168
  _LinkVersion = 1
FEATURE [App::Link] D1_LED_0603_1608Metric_cfe29d252c61_ln_003  label="D3_LED_0603_1608Metric_9c48ebd8f9c8"
  AutoLinkLabel = true
  AutoPlacement = true
  LinkPlacement = pos=(52.5,-36.2875,0) rot=(0,0,1;1.5708rad)
  LinkedObject = -> Shape005
  Placement = pos=(52.5,-36.2875,0) rot=(0,0,1;1.5708rad)
  SyncGroupVisibility = false
  TreeRank = 169
  _LinkVersion = 1
FEATURE [App::Link] C99_C_0402_1005Metric_0b61def5e92b_ln_031  label="C69_C_0402_1005Metric_ebf2f8d97770"
  AutoLinkLabel = true
  AutoPlacement = true
  LinkPlacement = pos=(34.48,-46,0) rot=(0,0,1;0rad)
  LinkedObject = -> Shape003
  Placement = pos=(34.48,-46,0) rot=(0,0,1;0rad)
  SyncGroupVisibility = false
  TreeRank = 170
  _LinkVersion = 1
FEATURE [App::Link] C99_C_0402_1005Metric_0b61def5e92b_ln_032  label="C43_C_0402_1005Metric_5057f7783708"
  AutoLinkLabel = true
  AutoPlacement = true
  LinkPlacement = pos=(31.7,-58.82,0) rot=(0,0,1;1.5708rad)
  LinkedObject = -> Shape003
  Placement = pos=(31.7,-58.82,0) rot=(0,0,1;1.5708rad)
  SyncGroupVisibility = false
  TreeRank = 171
  _LinkVersion = 1
FEATURE [App::Link] C12_C_0603_1608Metric_8642f7516920_ln_015  label="C6_C_0603_1608Metric_f1acf472f804"
  AutoLinkLabel = true
  AutoPlacement = true
  LinkPlacement = pos=(25.875,-10.4,0) rot=(0,0,1;3.14159rad)
  LinkedObject = -> Shape002
  Placement = pos=(25.875,-10.4,0) rot=(0,0,1;3.14159rad)
  SyncGroupVisibility = false
  TreeRank = 172
  _LinkVersion = 1
FEATURE [App::Link] R35_R_0402_1005Metric_f5f3ad6d96c7_ln_008  label="R5_R_0402_1005Metric_3468b1f7b807"
  AutoLinkLabel = true
  AutoPlacement = true
  LinkPlacement = pos=(51.7,-38.715,0) rot=(0,0,1;1.5708rad)
  LinkedObject = -> Shape
  Placement = pos=(51.7,-38.715,0) rot=(0,0,1;1.5708rad)
  SyncGroupVisibility = false
  TreeRank = 173
  _LinkVersion = 1
FEATURE [App::Link] L20_L_0402_1005Metric_fefcc591d3d4_ln_021  label="L29_L_0402_1005Metric_28eb01517140"
  AutoLinkLabel = true
  AutoPlacement = true
  LinkPlacement = pos=(13.905,-12.6,0) rot=(0,0,1;0rad)
  LinkedObject = -> Shape004
  Placement = pos=(13.905,-12.6,0) rot=(0,0,1;0rad)
  SyncGroupVisibility = false
  TreeRank = 174
  _LinkVersion = 1
FEATURE [Part::Feature] Shape011  label="U7_SOT_23_5_c46f7dd765f9"
  FixShape = 1
  InvalidShape = false
  Placement = pos=(54.3,-40.175,0) rot=(0,0,1;3.14159rad)
  TreeRank = 176
  ValidateShape = false
  shape: bbox 2.8 x 2.9 x 1.55 mm, 109 faces (baked)
FEATURE [App::Link] C12_C_0603_1608Metric_8642f7516920_ln_016  label="C2_C_0603_1608Metric_29d59376f99a"
  AutoLinkLabel = true
  AutoPlacement = true
  LinkPlacement = pos=(57.15,-40.3,0) rot=(0,0,-1;1.5708rad)
  LinkedObject = -> Shape002
  Placement = pos=(57.15,-40.3,0) rot=(0,0,-1;1.5708rad)
  SyncGroupVisibility = false
  TreeRank = 177
  _LinkVersion = 1
FEATURE [App::Link] C99_C_0402_1005Metric_0b61def5e92b_ln_033  label="C49_C_0402_1005Metric_ba87de366442"
  AutoLinkLabel = true
  AutoPlacement = true
  LinkPlacement = pos=(71.23,-56.9,0) rot=(0,0,1;0rad)
  LinkedObject = -> Shape003
  Placement = pos=(71.23,-56.9,0) rot=(0,0,1;0rad)
  SyncGroupVisibility = false
  TreeRank = 178
  _LinkVersion = 1
FEATURE [App::Link] C99_C_0402_1005Metric_0b61def5e92b_ln_034  label="C11_C_0402_1005Metric_c6aad14027c4"
  AutoLinkLabel = true
  AutoPlacement = true
  LinkPlacement = pos=(9.97,-13.93,0) rot=(0,0,1;1.5708rad)
  LinkedObject = -> Shape003
  Placement = pos=(9.97,-13.93,0) rot=(0,0,1;1.5708rad)
  SyncGroupVisibility = false
  TreeRank = 179
  _LinkVersion = 1
FEATURE [App::Link] C99_C_0402_1005Metric_0b61def5e92b_ln_035  label="C68_C_0402_1005Metric_adf72fb77db9"
  AutoLinkLabel = true
  AutoPlacement = true
  LinkPlacement = pos=(37,-59.38,0) rot=(0,0,-1;1.5708rad)
  LinkedObject = -> Shape003
  Placement = pos=(37,-59.38,0) rot=(0,0,-1;1.5708rad)
  SyncGroupVisibility = false
  TreeRank = 180
  _LinkVersion = 1
FEATURE [App::Link] C99_C_0402_1005Metric_0b61def5e92b_ln_036  label="C37_C_0402_1005Metric_dfa3128dd12b"
  AutoLinkLabel = true
  AutoPlacement = true
  LinkPlacement = pos=(34,-25.68,0) rot=(0,0,1;1.5708rad)
  LinkedObject = -> Shape003
  Placement = pos=(34,-25.68,0) rot=(0,0,1;1.5708rad)
  SyncGroupVisibility = false
  TreeRank = 181
  _LinkVersion = 1
FEATURE [App::Link] L20_L_0402_1005Metric_fefcc591d3d4_ln_022  label="L5_L_0402_1005Metric_39a68276db58"
  AutoLinkLabel = true
  AutoPlacement = true
  LinkPlacement = pos=(41.42,-12,0) rot=(0,0,1;0rad)
  LinkedObject = -> Shape004
  Placement = pos=(41.42,-12,0) rot=(0,0,1;0rad)
  SyncGroupVisibility = false
  TreeRank = 182
  _LinkVersion = 1
FEATURE [App::Link] L6_L_0603_1608Metric_c72d023e8189_ln_  label="L1_L_0603_1608Metric_0fae2e62cd60"
  AutoLinkLabel = true
  AutoPlacement = true
  LinkPlacement = pos=(11.2,-19.2,0) rot=(0,0,1;3.14159rad)
  LinkedObject = -> Shape008
  Placement = pos=(11.2,-19.2,0) rot=(0,0,1;3.14159rad)
  SyncGroupVisibility = false
  TreeRank = 183
  _LinkVersion = 1
FEATURE [App::Link] C12_C_0603_1608Metric_8642f7516920_ln_017  label="C13_C_0603_1608Metric_902ac20b3911"
  AutoLinkLabel = true
  AutoPlacement = true
  LinkPlacement = pos=(44.125,-42.725,0) rot=(0,0,1;0rad)
  LinkedObject = -> Shape002
  Placement = pos=(44.125,-42.725,0) rot=(0,0,1;0rad)
  SyncGroupVisibility = false
  TreeRank = 184
  _LinkVersion = 1
FEATURE [App::Link] D1_LED_0603_1608Metric_cfe29d252c61_ln_004  label="D4_LED_0603_1608Metric_978ad23d8b9f"
  AutoLinkLabel = true
  AutoPlacement = true
  LinkPlacement = pos=(55.5,-36.2875,0) rot=(0,0,1;1.5708rad)
  LinkedObject = -> Shape005
  Placement = pos=(55.5,-36.2875,0) rot=(0,0,1;1.5708rad)
  SyncGroupVisibility = false
  TreeRank = 185
  _LinkVersion = 1
FEATURE [App::Link] C99_C_0402_1005Metric_0b61def5e92b_ln_037  label="C71_C_0402_1005Metric_8e5e6772e0df"
  AutoLinkLabel = true
  AutoPlacement = true
  LinkPlacement = pos=(15.17,-13.93,0) rot=(0,0,1;1.5708rad)
  LinkedObject = -> Shape003
  Placement = pos=(15.17,-13.93,0) rot=(0,0,1;1.5708rad)
  SyncGroupVisibility = false
  TreeRank = 186
  _LinkVersion = 1
FEATURE [App::Link] C12_C_0603_1608Metric_8642f7516920_ln_018  label="C14_C_0603_1608Metric_7ae83664b820"
  AutoLinkLabel = true
  AutoPlacement = true
  LinkPlacement = pos=(50.925,-42.725,0) rot=(0,0,1;0rad)
  LinkedObject = -> Shape002
  Placement = pos=(50.925,-42.725,0) rot=(0,0,1;0rad)
  SyncGroupVisibility = false
  TreeRank = 187
  _LinkVersion = 1
FEATURE [App::Link] C99_C_0402_1005Metric_0b61def5e92b_ln_038  label="C70_C_0402_1005Metric_e5a1ae6d6584"
  AutoLinkLabel = true
  AutoPlacement = true
  LinkPlacement = pos=(12.57,-13.93,0) rot=(0,0,1;1.5708rad)
  LinkedObject = -> Shape003
  Placement = pos=(12.57,-13.93,0) rot=(0,0,1;1.5708rad)
  SyncGroupVisibility = false
  TreeRank = 188
  _LinkVersion = 1
FEATURE [App::Link] C12_C_0603_1608Metric_8642f7516920_ln_019  label="C59_C_0603_1608Metric_c4eca3a156d1"
  AutoLinkLabel = true
  AutoPlacement = true
  LinkPlacement = pos=(80.375,-10.365,0) rot=(0,0,1;3.14159rad)
  LinkedObject = -> Shape002
  Placement = pos=(80.375,-10.365,0) rot=(0,0,1;3.14159rad)
  SyncGroupVisibility = false
  TreeRank = 189
  _LinkVersion = 1
FEATURE [App::Link] R35_R_0402_1005Metric_f5f3ad6d96c7_ln_009  label="R22_R_0402_1005Metric_e3bbef54877c"
  AutoLinkLabel = true
  AutoPlacement = true
  LinkPlacement = pos=(11.3,-33.1,0) rot=(0,0,1;3.14159rad)
  LinkedObject = -> Shape
  Placement = pos=(11.3,-33.1,0) rot=(0,0,1;3.14159rad)
  SyncGroupVisibility = false
  TreeRank = 190
  _LinkVersion = 1
FEATURE [App::Link] C99_C_0402_1005Metric_0b61def5e92b_ln_039  label="C35_C_0402_1005Metric_6869360f5880"
  AutoLinkLabel = true
  AutoPlacement = true
  LinkPlacement = pos=(36.2,-10.48,0) rot=(0,0,1;1.5708rad)
  LinkedObject = -> Shape003
  Placement = pos=(36.2,-10.48,0) rot=(0,0,1;1.5708rad)
  SyncGroupVisibility = false
  TreeRank = 191
  _LinkVersion = 1
FEATURE [Part::Feature] Shape012  label="U6_QFN_56_1EP_7x7mm_P04mm_EP32x32mm_00caf949446c"
  FixShape = 1
  InvalidShape = false
  Placement = pos=(73.1,-34.1,0) rot=(0,0,1;3.14159rad)
  TreeRank = 193
  ValidateShape = false
  shape: bbox 7 x 7 x 0.95 mm, 350 faces (baked)
FEATURE [App::Link] C99_C_0402_1005Metric_0b61def5e92b_ln_040  label="C98_C_0402_1005Metric_ac914dad32c1"
  AutoLinkLabel = true
  AutoPlacement = true
  LinkPlacement = pos=(77.3,-26.6,0) rot=(0,0,-1;1.5708rad)
  LinkedObject = -> Shape003
  Placement = pos=(77.3,-26.6,0) rot=(0,0,-1;1.5708rad)
  SyncGroupVisibility = false
  TreeRank = 194
  _LinkVersion = 1
FEATURE [App::Link] C99_C_0402_1005Metric_0b61def5e92b_ln_041  label="C3_C_0402_1005Metric_ef1139b78acf"
  AutoLinkLabel = true
  AutoPlacement = true
  LinkPlacement = pos=(31.3,-10.98,0) rot=(0,0,-1;1.5708rad)
  LinkedObject = -> Shape003
  Placement = pos=(31.3,-10.98,0) rot=(0,0,-1;1.5708rad)
  SyncGroupVisibility = false
  TreeRank = 195
  _LinkVersion = 1
FEATURE [App::Link] R35_R_0402_1005Metric_f5f3ad6d96c7_ln_010  label="R34_R_0402_1005Metric_5615e024c238"
  AutoLinkLabel = true
  AutoPlacement = true
  LinkPlacement = pos=(66.5,-37.6,0) rot=(0,0,1;1.5708rad)
  LinkedObject = -> Shape
  Placement = pos=(66.5,-37.6,0) rot=(0,0,1;1.5708rad)
  SyncGroupVisibility = false
  TreeRank = 196
  _LinkVersion = 1
FEATURE [App::Link] L20_L_0402_1005Metric_fefcc591d3d4_ln_023  label="L33_L_0402_1005Metric_a440f87068b8"
  AutoLinkLabel = true
  AutoPlacement = true
  LinkPlacement = pos=(9.97,-55.965,0) rot=(0,0,1;1.5708rad)
  LinkedObject = -> Shape004
  Placement = pos=(9.97,-55.965,0) rot=(0,0,1;1.5708rad)
  SyncGroupVisibility = false
  TreeRank = 197
  _LinkVersion = 1
FEATURE [App::Link] U19_CQ_assembly_0c48127af4d7_ln_001  label="U17_CQ assembly_09b4001c005a"
  AutoLinkLabel = true
  AutoPlacement = true
  LinkPlacement = pos=(21.8,-10.9275,0) rot=(0,0,1;1.5708rad)
  LinkedObject = -> Part004
  Placement = pos=(21.8,-10.9275,0) rot=(0,0,1;1.5708rad)
  SyncGroupVisibility = false
  TreeRank = 198
  _LinkVersion = 1
FEATURE [App::Link] C12_C_0603_1608Metric_8642f7516920_ln_020  label="C1_C_0603_1608Metric_81cba5b497cb"
  AutoLinkLabel = true
  AutoPlacement = true
  LinkPlacement = pos=(25.875,-7.4,0) rot=(0,0,1;3.14159rad)
  LinkedObject = -> Shape002
  Placement = pos=(25.875,-7.4,0) rot=(0,0,1;3.14159rad)
  SyncGroupVisibility = false
  TreeRank = 199
  _LinkVersion = 1
FEATURE [App::Link] C99_C_0402_1005Metric_0b61def5e92b_ln_042  label="C29_C_0402_1005Metric_812c78cc34dd"
  AutoLinkLabel = true
  AutoPlacement = true
  LinkPlacement = pos=(43.32,-12,0) rot=(0,0,1;0rad)
  LinkedObject = -> Shape003
  Placement = pos=(43.32,-12,0) rot=(0,0,1;0rad)
  SyncGroupVisibility = false
  TreeRank = 200
  _LinkVersion = 1
FEATURE [App::Link] C12_C_0603_1608Metric_8642f7516920_ln_021  label="C33_C_0603_1608Metric_7dda9ef5ceed"
  AutoLinkLabel = true
  AutoPlacement = true
  LinkPlacement = pos=(6.3,-17.4,0) rot=(0,0,1;3.14159rad)
  LinkedObject = -> Shape002
  Placement = pos=(6.3,-17.4,0) rot=(0,0,1;3.14159rad)
  SyncGroupVisibility = false
  TreeRank = 201
  _LinkVersion = 1
FEATURE [App::Link] C99_C_0402_1005Metric_0b61def5e92b_ln_043  label="C47_C_0402_1005Metric_e5586804dad4"
  AutoLinkLabel = true
  AutoPlacement = true
  LinkPlacement = pos=(65.3,-12.7,0) rot=(0,0,1;0.785398rad)
  LinkedObject = -> Shape003
  Placement = pos=(65.3,-12.7,0) rot=(0,0,1;0.785398rad)
  SyncGroupVisibility = false
  TreeRank = 202
  _LinkVersion = 1
FEATURE [App::Link] C12_C_0603_1608Metric_8642f7516920_ln_022  label="C44_C_0603_1608Metric_fd3cfbcef1d2"
  AutoLinkLabel = true
  AutoPlacement = true
  LinkPlacement = pos=(61.3,-53.7,0) rot=(0,0,1;3.14159rad)
  LinkedObject = -> Shape002
  Placement = pos=(61.3,-53.7,0) rot=(0,0,1;3.14159rad)
  SyncGroupVisibility = false
  TreeRank = 203
  _LinkVersion = 1
FEATURE [App::Link] U19_CQ_assembly_0c48127af4d7_ln_002  label="U13_CQ assembly_d28a2e697678"
  AutoLinkLabel = true
  AutoPlacement = true
  LinkPlacement = pos=(58.4,-12.3275,0) rot=(0,0,1;1.5708rad)
  LinkedObject = -> Part004
  Placement = pos=(58.4,-12.3275,0) rot=(0,0,1;1.5708rad)
  SyncGroupVisibility = false
  TreeRank = 204
  _LinkVersion = 1
FEATURE [App::Link] D1_LED_0603_1608Metric_cfe29d252c61_ln_005  label="D5_LED_0603_1608Metric_926ae287a0ec"
  AutoLinkLabel = true
  AutoPlacement = true
  LinkPlacement = pos=(46.5,-33.2375,0) rot=(0,0,1;1.5708rad)
  LinkedObject = -> Shape005
  Placement = pos=(46.5,-33.2375,0) rot=(0,0,1;1.5708rad)
  SyncGroupVisibility = false
  TreeRank = 205
  _LinkVersion = 1
FEATURE [App::Link] C99_C_0402_1005Metric_0b61def5e92b_ln_044  label="C66_C_0402_1005Metric_23b8d208cb86"
  AutoLinkLabel = true
  AutoPlacement = true
  LinkPlacement = pos=(81.18,-12.6,0) rot=(0,0,1;0rad)
  LinkedObject = -> Shape003
  Placement = pos=(81.18,-12.6,0) rot=(0,0,1;0rad)
  SyncGroupVisibility = false
  TreeRank = 206
  _LinkVersion = 1
FEATURE [App::Link] L20_L_0402_1005Metric_fefcc591d3d4_ln_024  label="L8_L_0402_1005Metric_ee2305d67d17"
  AutoLinkLabel = true
  AutoPlacement = true
  LinkPlacement = pos=(24.9,-56.815,0) rot=(0,0,-1;1.5708rad)
  LinkedObject = -> Shape004
  Placement = pos=(24.9,-56.815,0) rot=(0,0,-1;1.5708rad)
  SyncGroupVisibility = false
  TreeRank = 207
  _LinkVersion = 1
FEATURE [App::Link] L20_L_0402_1005Metric_fefcc591d3d4_ln_025  label="L34_L_0402_1005Metric_c0144a991ba0"
  AutoLinkLabel = true
  AutoPlacement = true
  LinkPlacement = pos=(11.255,-57.3,0) rot=(0,0,1;0rad)
  LinkedObject = -> Shape004
  Placement = pos=(11.255,-57.3,0) rot=(0,0,1;0rad)
  SyncGroupVisibility = false
  TreeRank = 208
  _LinkVersion = 1
FEATURE [App::Link] R35_R_0402_1005Metric_f5f3ad6d96c7_ln_011  label="R4_R_0402_1005Metric_d4c8867b1f44"
  AutoLinkLabel = true
  AutoPlacement = true
  LinkPlacement = pos=(51.7,-40.615,0) rot=(0,0,1;1.5708rad)
  LinkedObject = -> Shape
  Placement = pos=(51.7,-40.615,0) rot=(0,0,1;1.5708rad)
  SyncGroupVisibility = false
  TreeRank = 209
  _LinkVersion = 1
FEATURE [App::Link] C99_C_0402_1005Metric_0b61def5e92b_ln_045  label="C39_C_0402_1005Metric_0a3de914835b"
  AutoLinkLabel = true
  AutoPlacement = true
  LinkPlacement = pos=(34,-44.5,0) rot=(0,0,-1;1.5708rad)
  LinkedObject = -> Shape003
  Placement = pos=(34,-44.5,0) rot=(0,0,-1;1.5708rad)
  SyncGroupVisibility = false
  TreeRank = 210
  _LinkVersion = 1
FEATURE [App::Link] C12_C_0603_1608Metric_8642f7516920_ln_023  label="C45_C_0603_1608Metric_8122c7cb9830"
  AutoLinkLabel = true
  AutoPlacement = true
  LinkPlacement = pos=(62.565,-10.635,0) rot=(0,0,1;3.14159rad)
  LinkedObject = -> Shape002
  Placement = pos=(62.565,-10.635,0) rot=(0,0,1;3.14159rad)
  SyncGroupVisibility = false
  TreeRank = 211
  _LinkVersion = 1
FEATURE [App::Link] R35_R_0402_1005Metric_f5f3ad6d96c7_ln_012  label="R1_R_0402_1005Metric_420fcc0bba52"
  AutoLinkLabel = true
  AutoPlacement = true
  LinkPlacement = pos=(44.9,-40.615,0) rot=(0,0,1;1.5708rad)
  LinkedObject = -> Shape
  Placement = pos=(44.9,-40.615,0) rot=(0,0,1;1.5708rad)
  SyncGroupVisibility = false
  TreeRank = 212
  _LinkVersion = 1
FEATURE [App::Link] L20_L_0402_1005Metric_fefcc591d3d4_ln_026  label="L38_L_0402_1005Metric_57da23dcb069"
  AutoLinkLabel = true
  AutoPlacement = true
  LinkPlacement = pos=(16.505,-57.3,0) rot=(0,0,1;0rad)
  LinkedObject = -> Shape004
  Placement = pos=(16.505,-57.3,0) rot=(0,0,1;0rad)
  SyncGroupVisibility = false
  TreeRank = 213
  _LinkVersion = 1
FEATURE [App::Link] C12_C_0603_1608Metric_8642f7516920_ln_024  label="C84_C_0603_1608Metric_5add88d28623"
  AutoLinkLabel = true
  AutoPlacement = true
  LinkPlacement = pos=(79.025,-51.9725,0) rot=(0,0,1;3.14159rad)
  LinkedObject = -> Shape002
  Placement = pos=(79.025,-51.9725,0) rot=(0,0,1;3.14159rad)
  SyncGroupVisibility = false
  TreeRank = 214
  _LinkVersion = 1
FEATURE [App::Link] R35_R_0402_1005Metric_f5f3ad6d96c7_ln_013  label="R14_R_0402_1005Metric_b22e37155927"
  AutoLinkLabel = true
  AutoPlacement = true
  LinkPlacement = pos=(51.15,-33.2375,0) rot=(0,0,-1;1.5708rad)
  LinkedObject = -> Shape
  Placement = pos=(51.15,-33.2375,0) rot=(0,0,-1;1.5708rad)
  SyncGroupVisibility = false
  TreeRank = 215
  _LinkVersion = 1
FEATURE [App::Link] R35_R_0402_1005Metric_f5f3ad6d96c7_ln_014  label="R8_R_0402_1005Metric_e0ecb0157d35"
  AutoLinkLabel = true
  AutoPlacement = true
  LinkPlacement = pos=(45.15,-36.2875,0) rot=(0,0,-1;1.5708rad)
  LinkedObject = -> Shape
  Placement = pos=(45.15,-36.2875,0) rot=(0,0,-1;1.5708rad)
  SyncGroupVisibility = false
  TreeRank = 216
  _LinkVersion = 1
FEATURE [App::Link] C12_C_0603_1608Metric_8642f7516920_ln_025  label="C46_C_0603_1608Metric_ab6b7a860cf6"
  AutoLinkLabel = true
  AutoPlacement = true
  LinkPlacement = pos=(62.565,-12.185,0) rot=(0,0,1;3.14159rad)
  LinkedObject = -> Shape002
  Placement = pos=(62.565,-12.185,0) rot=(0,0,1;3.14159rad)
  SyncGroupVisibility = false
  TreeRank = 217
  _LinkVersion = 1
FEATURE [App::Link] R35_R_0402_1005Metric_f5f3ad6d96c7_ln_015  label="R44_R_0402_1005Metric_6095da51a8eb"
  AutoLinkLabel = true
  AutoPlacement = true
  LinkPlacement = pos=(73.1,-26.89,0) rot=(0,0,-1;1.5708rad)
  LinkedObject = -> Shape
  Placement = pos=(73.1,-26.89,0) rot=(0,0,-1;1.5708rad)
  SyncGroupVisibility = false
  TreeRank = 218
  _LinkVersion = 1
FEATURE [App::Link] C12_C_0603_1608Metric_8642f7516920_ln_026  label="C86_C_0603_1608Metric_ed7d19446401"
  AutoLinkLabel = true
  AutoPlacement = true
  LinkPlacement = pos=(79.02,-53.5225,0) rot=(0,0,1;3.14159rad)
  LinkedObject = -> Shape002
  Placement = pos=(79.02,-53.5225,0) rot=(0,0,1;3.14159rad)
  SyncGroupVisibility = false
  TreeRank = 219
  _LinkVersion = 1
FEATURE [App::Link] R35_R_0402_1005Metric_f5f3ad6d96c7_ln_016  label="R36_R_0402_1005Metric_f2448ea40649"
  AutoLinkLabel = true
  AutoPlacement = true
  LinkPlacement = pos=(81.1813,-57.76,0) rot=(0,0,-1;1.5708rad)
  LinkedObject = -> Shape
  Placement = pos=(81.1813,-57.76,0) rot=(0,0,-1;1.5708rad)
  SyncGroupVisibility = false
  TreeRank = 220
  _LinkVersion = 1
FEATURE [Part::Feature] Shape013  label="U12_SOT_143_13a6a7517807"
  FixShape = 1
  InvalidShape = false
  Placement = pos=(33.73,-16.3,0) rot=(0,0,-1;1.5708rad)
  TreeRank = 222
  ValidateShape = false
  shape: bbox 2.9 x 2.8 x 1.2 mm, 94 faces (baked)
FEATURE [App::Link] C12_C_0603_1608Metric_8642f7516920_ln_027  label="C58_C_0603_1608Metric_ff5f373ce49d"
  AutoLinkLabel = true
  AutoPlacement = true
  LinkPlacement = pos=(80.37,-8.815,0) rot=(0,0,1;3.14159rad)
  LinkedObject = -> Shape002
  Placement = pos=(80.37,-8.815,0) rot=(0,0,1;3.14159rad)
  SyncGroupVisibility = false
  TreeRank = 223
  _LinkVersion = 1
FEATURE [App::Link] L20_L_0402_1005Metric_fefcc591d3d4_ln_027  label="L24_L_0402_1005Metric_2290206142fc"
  AutoLinkLabel = true
  AutoPlacement = true
  LinkPlacement = pos=(5.3,-58.885,0) rot=(0,0,1;1.5708rad)
  LinkedObject = -> Shape004
  Placement = pos=(5.3,-58.885,0) rot=(0,0,1;1.5708rad)
  SyncGroupVisibility = false
  TreeRank = 224
  _LinkVersion = 1
FEATURE [App::Link] R35_R_0402_1005Metric_f5f3ad6d96c7_ln_017  label="R3_R_0402_1005Metric_708d61d10309"
  AutoLinkLabel = true
  AutoPlacement = true
  LinkPlacement = pos=(82.7,-13.11,0) rot=(0,0,-1;1.5708rad)
  LinkedObject = -> Shape
  Placement = pos=(82.7,-13.11,0) rot=(0,0,-1;1.5708rad)
  SyncGroupVisibility = false
  TreeRank = 225
  _LinkVersion = 1
FEATURE [App::Link] L20_L_0402_1005Metric_fefcc591d3d4_ln_028  label="L31_L_0402_1005Metric_b96d136c237e"
  AutoLinkLabel = true
  AutoPlacement = true
  LinkPlacement = pos=(16.505,-12.6,0) rot=(0,0,1;0rad)
  LinkedObject = -> Shape004
  Placement = pos=(16.505,-12.6,0) rot=(0,0,1;0rad)
  SyncGroupVisibility = false
  TreeRank = 226
  _LinkVersion = 1
FEATURE [App::Link] C99_C_0402_1005Metric_0b61def5e92b_ln_046  label="C34_C_0402_1005Metric_771558acb01f"
  AutoLinkLabel = true
  AutoPlacement = true
  LinkPlacement = pos=(52.92,-12,0) rot=(0,0,1;0rad)
  LinkedObject = -> Shape003
  Placement = pos=(52.92,-12,0) rot=(0,0,1;0rad)
  SyncGroupVisibility = false
  TreeRank = 227
  _LinkVersion = 1
FEATURE [App::Link] U19_CQ_assembly_0c48127af4d7_ln_003  label="U21_CQ assembly_16b47658897b"
  AutoLinkLabel = true
  AutoPlacement = true
  LinkPlacement = pos=(74.95,-55.3,0) rot=(0,0,1;1.5708rad)
  LinkedObject = -> Part004
  Placement = pos=(74.95,-55.3,0) rot=(0,0,1;1.5708rad)
  SyncGroupVisibility = false
  TreeRank = 228
  _LinkVersion = 1
FEATURE [App::Link] C12_C_0603_1608Metric_8642f7516920_ln_028  label="C75_C_0603_1608Metric_bb64ba6c0d59"
  AutoLinkLabel = true
  AutoPlacement = true
  LinkPlacement = pos=(61.3,-55.2,0) rot=(0,0,1;3.14159rad)
  LinkedObject = -> Shape002
  Placement = pos=(61.3,-55.2,0) rot=(0,0,1;3.14159rad)
  SyncGroupVisibility = false
  TreeRank = 229
  _LinkVersion = 1
FEATURE [App::Link] L20_L_0402_1005Metric_fefcc591d3d4_ln_029  label="L23_L_0402_1005Metric_91fafefdec7a"
  AutoLinkLabel = true
  AutoPlacement = true
  LinkPlacement = pos=(12.57,-11.265,0) rot=(0,0,1;1.5708rad)
  LinkedObject = -> Shape004
  Placement = pos=(12.57,-11.265,0) rot=(0,0,1;1.5708rad)
  SyncGroupVisibility = false
  TreeRank = 230
  _LinkVersion = 1
FEATURE [App::Link] L20_L_0402_1005Metric_fefcc591d3d4_ln_030  label="L11_L_0402_1005Metric_6d8c2ff64333"
  AutoLinkLabel = true
  AutoPlacement = true
  LinkPlacement = pos=(49.57,-12.95,0) rot=(0,0,1;1.5708rad)
  LinkedObject = -> Shape004
  Placement = pos=(49.57,-12.95,0) rot=(0,0,1;1.5708rad)
  SyncGroupVisibility = false
  TreeRank = 231
  _LinkVersion = 1
FEATURE [App::Link] D1_LED_0603_1608Metric_cfe29d252c61_ln_006  label="D7_LED_0603_1608Metric_404e0079a0fb"
  AutoLinkLabel = true
  AutoPlacement = true
  LinkPlacement = pos=(52.5,-33.2375,0) rot=(0,0,1;1.5708rad)
  LinkedObject = -> Shape005
  Placement = pos=(52.5,-33.2375,0) rot=(0,0,1;1.5708rad)
  SyncGroupVisibility = false
  TreeRank = 232
  _LinkVersion = 1
FEATURE [App::Link] R35_R_0402_1005Metric_f5f3ad6d96c7_ln_018  label="R11_R_0402_1005Metric_b1c508115d17"
  AutoLinkLabel = true
  AutoPlacement = true
  LinkPlacement = pos=(54.15,-36.2875,0) rot=(0,0,-1;1.5708rad)
  LinkedObject = -> Shape
  Placement = pos=(54.15,-36.2875,0) rot=(0,0,-1;1.5708rad)
  SyncGroupVisibility = false
  TreeRank = 233
  _LinkVersion = 1
FEATURE [App::Link] U19_CQ_assembly_0c48127af4d7_ln_004  label="U18_CQ assembly_86235c56fa26"
  AutoLinkLabel = true
  AutoPlacement = true
  LinkPlacement = pos=(21.8,-55.6275,0) rot=(0,0,1;1.5708rad)
  LinkedObject = -> Part004
  Placement = pos=(21.8,-55.6275,0) rot=(0,0,1;1.5708rad)
  SyncGroupVisibility = false
  TreeRank = 234
  _LinkVersion = 1
FEATURE [App::Link] R35_R_0402_1005Metric_f5f3ad6d96c7_ln_019  label="R23_R_0402_1005Metric_e2ed9d9b06ae"
  AutoLinkLabel = true
  AutoPlacement = true
  LinkPlacement = pos=(12.8,-33.6,0) rot=(0,0,1;1.5708rad)
  LinkedObject = -> Shape
  Placement = pos=(12.8,-33.6,0) rot=(0,0,1;1.5708rad)
  SyncGroupVisibility = false
  TreeRank = 235
  _LinkVersion = 1
FEATURE [App::Link] R35_R_0402_1005Metric_f5f3ad6d96c7_ln_020  label="R2_R_0402_1005Metric_e7ea086e2c45"
  AutoLinkLabel = true
  AutoPlacement = true
  LinkPlacement = pos=(44.9,-38.715,0) rot=(0,0,1;1.5708rad)
  LinkedObject = -> Shape
  Placement = pos=(44.9,-38.715,0) rot=(0,0,1;1.5708rad)
  SyncGroupVisibility = false
  TreeRank = 236
  _LinkVersion = 1
FEATURE [App::Link] C99_C_0402_1005Metric_0b61def5e92b_ln_047  label="C88_C_0402_1005Metric_a61bc33b85cf"
  AutoLinkLabel = true
  AutoPlacement = true
  LinkPlacement = pos=(80.0563,-15.805,0) rot=(0,0,-1;1.5708rad)
  LinkedObject = -> Shape003
  Placement = pos=(80.0563,-15.805,0) rot=(0,0,-1;1.5708rad)
  SyncGroupVisibility = false
  TreeRank = 237
  _LinkVersion = 1
FEATURE [Part::Feature] Shape014  label="U3_SOT_23_b6f0decfda9a"
  FixShape = 1
  InvalidShape = false
  Placement = pos=(50.7625,-28.775,0) rot=(0,0,1;3.14159rad)
  TreeRank = 239
  ValidateShape = false
  shape: bbox 2.5 x 3 x 1.2 mm, 76 faces (baked)
FEATURE [App::Link] L20_L_0402_1005Metric_fefcc591d3d4_ln_031  label="L15_L_0402_1005Metric_15e2c9c0520b"
  AutoLinkLabel = true
  AutoPlacement = true
  LinkPlacement = pos=(61.54,-13.9,0) rot=(0,0,-1;1.5708rad)
  LinkedObject = -> Shape004
  Placement = pos=(61.54,-13.9,0) rot=(0,0,-1;1.5708rad)
  SyncGroupVisibility = false
  TreeRank = 240
  _LinkVersion = 1
FEATURE [App::Link] L20_L_0402_1005Metric_fefcc591d3d4_ln_032  label="L36_L_0402_1005Metric_86cd0f7a4665"
  AutoLinkLabel = true
  AutoPlacement = true
  LinkPlacement = pos=(13.905,-57.3,0) rot=(0,0,1;0rad)
  LinkedObject = -> Shape004
  Placement = pos=(13.905,-57.3,0) rot=(0,0,1;0rad)
  SyncGroupVisibility = false
  TreeRank = 241
  _LinkVersion = 1
FEATURE [App::Link] R35_R_0402_1005Metric_f5f3ad6d96c7_ln_021  label="R10_R_0402_1005Metric_5ca2393d4e02"
  AutoLinkLabel = true
  AutoPlacement = true
  LinkPlacement = pos=(51.15,-36.2875,0) rot=(0,0,-1;1.5708rad)
  LinkedObject = -> Shape
  Placement = pos=(51.15,-36.2875,0) rot=(0,0,-1;1.5708rad)
  SyncGroupVisibility = false
  TreeRank = 242
  _LinkVersion = 1
FEATURE [App::Link] U12_SOT_143_13a6a7517807_ln_  label="U25_SOT_143_4ab4e93d02a0"
  AutoLinkLabel = true
  AutoPlacement = true
  LinkPlacement = pos=(34.2,-53.61,0) rot=(0,0,1;1.5708rad)
  LinkedObject = -> Shape013
  Placement = pos=(34.2,-53.61,0) rot=(0,0,1;1.5708rad)
  SyncGroupVisibility = false
  TreeRank = 243
  _LinkVersion = 1
FEATURE [App::Link] U7_SOT_23_5_c46f7dd765f9_ln_  label="U5_SOT_23_5_6eb0f90d23b4"
  AutoLinkLabel = true
  AutoPlacement = true
  LinkPlacement = pos=(47.55,-40.175,0) rot=(0,0,1;3.14159rad)
  LinkedObject = -> Shape011
  Placement = pos=(47.55,-40.175,0) rot=(0,0,1;3.14159rad)
  SyncGroupVisibility = false
  TreeRank = 244
  _LinkVersion = 1
FEATURE [App::Part] Top_5cf6
  ClaimAllChildren = false
  ExportMode = 1
  Group = -> [Shape,R35_R_0402_1005Metric_f5f3ad6d96c7_ln_,Shape001,Shape002,Shape003,C99_C_0402_1005Metric_0b61def5e92b_ln_,C12_C_0603_1608Metric_8642f7516920_ln_,Shape004,L20_L_0402_1005Metric_fefcc591d3d4_ln_,L20_L_0402_1005Metric_fefcc591d3d4_ln_001,C99_C_0402_1005Metric_0b61def5e92b_ln_001,C99_C_0402_1005Metric_0b61def5e92b_ln_002,L20_L_0402_1005Metric_fefcc591d3d4_ln_002,+153 more]
  Origin = -> Origin003
  TreeRank = 24
  _ExportChildren = -> [Shape,R35_R_0402_1005Metric_f5f3ad6d96c7_ln_,Shape001,Shape002,Shape003,C99_C_0402_1005Metric_0b61def5e92b_ln_,C12_C_0603_1608Metric_8642f7516920_ln_,Shape004,L20_L_0402_1005Metric_fefcc591d3d4_ln_,L20_L_0402_1005Metric_fefcc591d3d4_ln_001,C99_C_0402_1005Metric_0b61def5e92b_ln_001,C99_C_0402_1005Metric_0b61def5e92b_ln_002,L20_L_0402_1005Metric_fefcc591d3d4_ln_002,+153 more]
  _GroupVersion = 1
FEATURE [App::Link] C12_C_0603_1608Metric_8642f7516920_ln_029  label="C20_C_0603_1608Metric_5f6bac0ac200"
  AutoLinkLabel = true
  AutoPlacement = true
  LinkPlacement = pos=(72,-37.705,-1.7702) rot=(0.707107,-0.707107,0;3.14159rad)
  LinkedObject = -> Shape002
  Placement = pos=(72,-37.705,-1.7702) rot=(0.707107,-0.707107,0;3.14159rad)
  SyncGroupVisibility = false
  TreeRank = 245
  _LinkVersion = 1
FEATURE [App::Link] C99_C_0402_1005Metric_0b61def5e92b_ln_048  label="C18_C_0402_1005Metric_0d8bc6ebe621"
  AutoLinkLabel = true
  AutoPlacement = true
  LinkPlacement = pos=(75.3,-37.21,-1.7702) rot=(0.707107,0.707107,0;3.14159rad)
  LinkedObject = -> Shape003
  Placement = pos=(75.3,-37.21,-1.7702) rot=(0.707107,0.707107,0;3.14159rad)
  SyncGroupVisibility = false
  TreeRank = 246
  _LinkVersion = 1
FEATURE [App::Link] C99_C_0402_1005Metric_0b61def5e92b_ln_049  label="C27_C_0402_1005Metric_a4d209a5c3fe"
  AutoLinkLabel = true
  AutoPlacement = true
  LinkPlacement = pos=(76.8,-35.7,-1.7702) rot=(0,1,0;3.14159rad)
  LinkedObject = -> Shape003
  Placement = pos=(76.8,-35.7,-1.7702) rot=(0,1,0;3.14159rad)
  SyncGroupVisibility = false
  TreeRank = 247
  _LinkVersion = 1
FEATURE [App::Link] C99_C_0402_1005Metric_0b61def5e92b_ln_050  label="C28_C_0402_1005Metric_6a91bc111ceb"
  AutoLinkLabel = true
  AutoPlacement = true
  LinkPlacement = pos=(72.9,-31.15,-1.7702) rot=(0.707107,-0.707107,0;3.14159rad)
  LinkedObject = -> Shape003
  Placement = pos=(72.9,-31.15,-1.7702) rot=(0.707107,-0.707107,0;3.14159rad)
  SyncGroupVisibility = false
  TreeRank = 248
  _LinkVersion = 1
FEATURE [App::Link] C99_C_0402_1005Metric_0b61def5e92b_ln_051  label="C26_C_0402_1005Metric_b1b0803f89ae"
  AutoLinkLabel = true
  AutoPlacement = true
  LinkPlacement = pos=(69.4,-33.13,-1.7702) rot=(1,0,0;3.14159rad)
  LinkedObject = -> Shape003
  Placement = pos=(69.4,-33.13,-1.7702) rot=(1,0,0;3.14159rad)
  SyncGroupVisibility = false
  TreeRank = 249
  _LinkVersion = 1
FEATURE [App::Link] C99_C_0402_1005Metric_0b61def5e92b_ln_052  label="C24_C_0402_1005Metric_8561940ff5c9"
  AutoLinkLabel = true
  AutoPlacement = true
  LinkPlacement = pos=(76.12,-33.13,-1.7702) rot=(0,1,0;3.14159rad)
  LinkedObject = -> Shape003
  Placement = pos=(76.12,-33.13,-1.7702) rot=(0,1,0;3.14159rad)
  SyncGroupVisibility = false
  TreeRank = 250
  _LinkVersion = 1
FEATURE [App::Link] C12_C_0603_1608Metric_8642f7516920_ln_030  label="C22_C_0603_1608Metric_33c540f53bb4"
  AutoLinkLabel = true
  AutoPlacement = true
  LinkPlacement = pos=(70.45,-37.7,-1.7702) rot=(0.707107,-0.707107,0;3.14159rad)
  LinkedObject = -> Shape002
  Placement = pos=(70.45,-37.7,-1.7702) rot=(0.707107,-0.707107,0;3.14159rad)
  SyncGroupVisibility = false
  TreeRank = 251
  _LinkVersion = 1
FEATURE [App::Link] C99_C_0402_1005Metric_0b61def5e92b_ln_053  label="C25_C_0402_1005Metric_79042a340dde"
  AutoLinkLabel = true
  AutoPlacement = true
  LinkPlacement = pos=(76.3,-37.21,-1.7702) rot=(0.707107,0.707107,0;3.14159rad)
  LinkedObject = -> Shape003
  Placement = pos=(76.3,-37.21,-1.7702) rot=(0.707107,0.707107,0;3.14159rad)
  SyncGroupVisibility = false
  TreeRank = 252
  _LinkVersion = 1
FEATURE [App::Link] C99_C_0402_1005Metric_0b61def5e92b_ln_054  label="C19_C_0402_1005Metric_22f3058224a2"
  AutoLinkLabel = true
  AutoPlacement = true
  LinkPlacement = pos=(71.9,-31.15,-1.7702) rot=(0.707107,0.707107,0;3.14159rad)
  LinkedObject = -> Shape003
  Placement = pos=(71.9,-31.15,-1.7702) rot=(0.707107,0.707107,0;3.14159rad)
  SyncGroupVisibility = false
  TreeRank = 253
  _LinkVersion = 1
FEATURE [App::Part] Bot_5cf6
  ClaimAllChildren = false
  ExportMode = 1
  Group = -> [C12_C_0603_1608Metric_8642f7516920_ln_029,C99_C_0402_1005Metric_0b61def5e92b_ln_048,C99_C_0402_1005Metric_0b61def5e92b_ln_049,C99_C_0402_1005Metric_0b61def5e92b_ln_050,C99_C_0402_1005Metric_0b61def5e92b_ln_051,C99_C_0402_1005Metric_0b61def5e92b_ln_052,C12_C_0603_1608Metric_8642f7516920_ln_030,C99_C_0402_1005Metric_0b61def5e92b_ln_053,C99_C_0402_1005Metric_0b61def5e92b_ln_054]
  Origin = -> Origin004
  TreeRank = 26
  _ExportChildren = -> [C12_C_0603_1608Metric_8642f7516920_ln_029,C99_C_0402_1005Metric_0b61def5e92b_ln_048,C99_C_0402_1005Metric_0b61def5e92b_ln_049,C99_C_0402_1005Metric_0b61def5e92b_ln_050,C99_C_0402_1005Metric_0b61def5e92b_ln_051,C99_C_0402_1005Metric_0b61def5e92b_ln_052,C12_C_0603_1608Metric_8642f7516920_ln_030,C99_C_0402_1005Metric_0b61def5e92b_ln_053,C99_C_0402_1005Metric_0b61def5e92b_ln_054]
  _GroupVersion = 1
FEATURE [App::Part] Step_Models_5cf6
  ClaimAllChildren = false
  ExportMode = 1
  Group = -> [Top_5cf6,Bot_5cf6]
  Origin = -> Origin002
  TreeRank = 36
  _ExportChildren = -> [Top_5cf6,Bot_5cf6]
  _GroupVersion = 1
FEATURE [Part::Feature] pads_area001  label="topPads_5cf6"
  FixShape = 1
  InvalidShape = false
  Placement = pos=(-99,65.045,0.02) rot=(0,0,1;0rad)
  TreeRank = 3346
  ValidateShape = false
  shape: bbox 88 x 69.5 x 2e-07 mm, 1489 faces, 0 solids (baked)
FEATURE [Part::Feature] Shape015001  label="topTracks_5cf6"
  FixShape = 1
  InvalidShape = false
  Placement = pos=(-99,65.045,0.01) rot=(0,0,1;0rad)
  TreeRank = 3387
  ValidateShape = false
  shape: bbox 84.65 x 57.38 x 2e-07 mm, 185 faces, 0 solids (baked)
FEATURE [Part::Feature] zones_area001  label="topZones_5cf6"
  FixShape = 1
  InvalidShape = false
  Placement = pos=(-99,65.045,0.01) rot=(0,0,1;0rad)
  TreeRank = 3456
  ValidateShape = false
  shape: bbox 87.29 x 69.29 x 2e-07 mm, 16 faces, 0 solids (baked)
FEATURE [Part::Feature] pads_area002001  label="botPads_5cf6"
  FixShape = 1
  InvalidShape = false
  Placement = pos=(-99,65.045,-1.7902) rot=(0,0,1;0rad)
  TreeRank = 4280
  ValidateShape = false
  shape: bbox 88 x 69.5 x 2e-07 mm, 1148 faces, 0 solids (baked)
FEATURE [Part::Feature] Shape015002001  label="botTracks_5cf6"
  FixShape = 1
  InvalidShape = false
  Placement = pos=(-99,65.045,-1.7802) rot=(0,0,1;0rad)
  TreeRank = 4301
  ValidateShape = false
  shape: bbox 66.63 x 56.41 x 2e-07 mm, 26 faces, 0 solids (baked)
FEATURE [Part::Feature] zones_area002001  label="botZones_5cf6"
  FixShape = 1
  InvalidShape = false
  Placement = pos=(-99,65.045,-1.7802) rot=(0,0,1;0rad)
  TreeRank = 4320
  ValidateShape = false
  shape: bbox 87.29 x 69.29 x 2e-07 mm, 3 faces, 0 solids (baked)
FEATURE [App::Part] Board_Geoms_5cf6
  ClaimAllChildren = false
  ExportMode = 1
  Group = -> [Pcb_5cf6,PCB_Sketch_5cf6,pads_area001,Shape015001,zones_area001,pads_area002001,Shape015002001,zones_area002001]
  Origin = -> Origin
  TreeRank = 19
  _ExportChildren = -> [Pcb_5cf6,PCB_Sketch_5cf6,pads_area001,Shape015001,zones_area001,pads_area002001,Shape015002001,zones_area002001]
  _GroupVersion = 1
FEATURE [App::Part] Board_5cf6  label="GreX Frontend"
  ClaimAllChildren = false
  ExportMode = 1
  Group = -> [Local_CS_5cf6,Board_Geoms_5cf6,Step_Models_5cf6]
  Origin = -> Origin001
  TreeRank = 21
  _ExportChildren = -> [Local_CS_5cf6,Board_Geoms_5cf6,Step_Models_5cf6]
  _GroupVersion = 1
